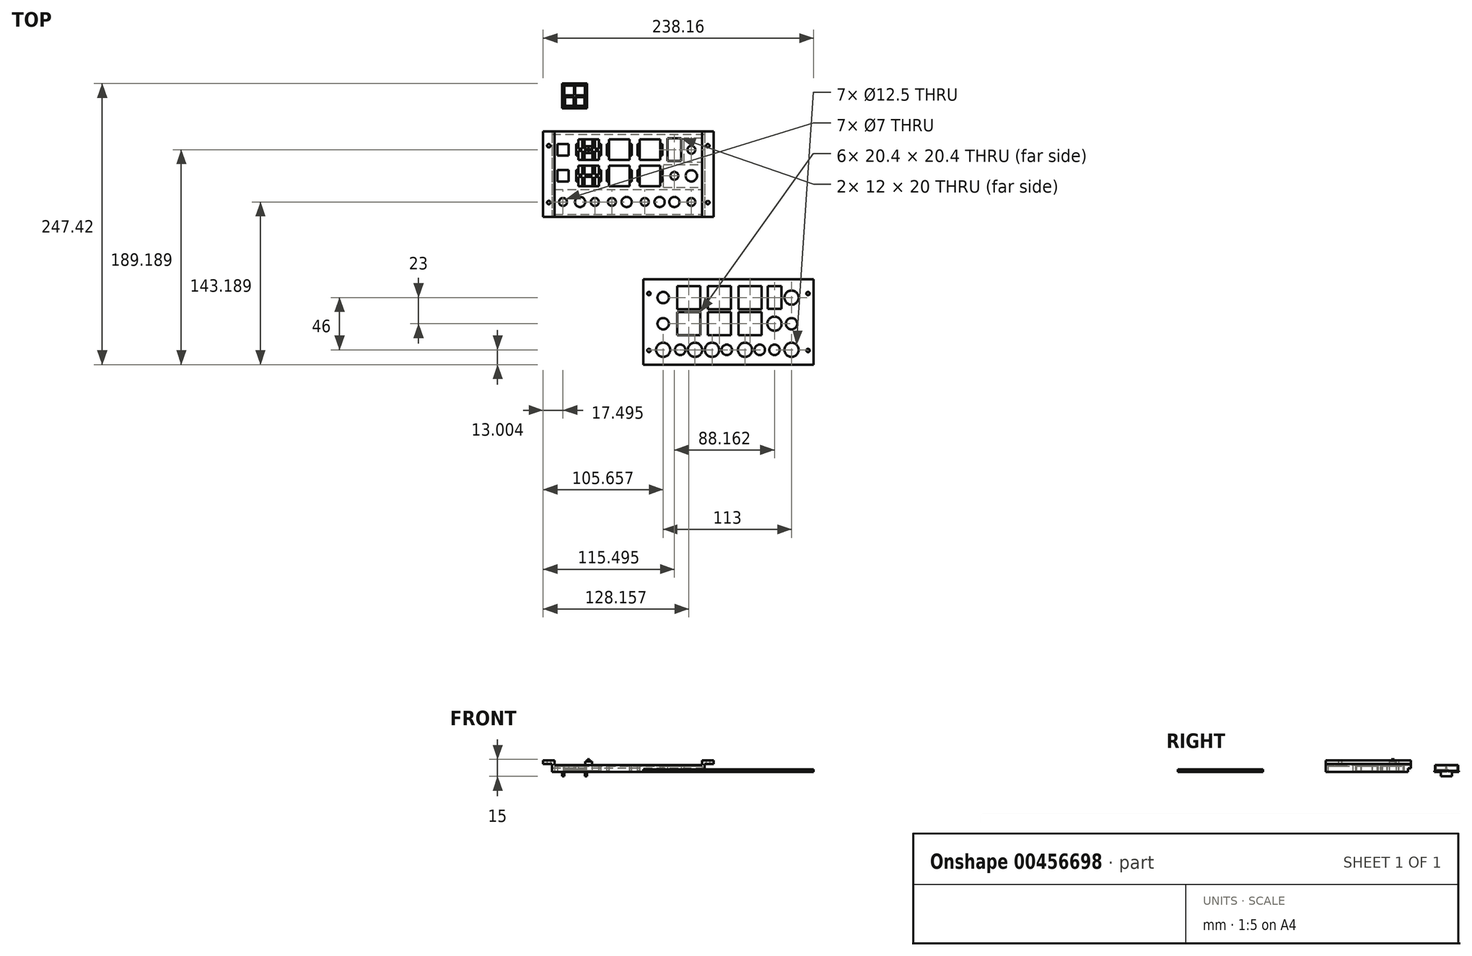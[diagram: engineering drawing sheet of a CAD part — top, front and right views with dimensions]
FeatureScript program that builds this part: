
annotation { "Feature Type Name" : "Feature", "Feature Type Description" : "" }
export const myFeature = defineFeature(function(context is Context, id is Id, definition is map)
    precondition{}
    {
        {
            var Q0;
            Q0=qCreatedBy(makeId("Top.planeOp"),FACE);
            var sketch = newSketch(context, id + "F0", { "sketchPlane" : qUnion([Q0])});
            skLineSegment(sketch, "E0.bottom", {"start": v(0.5, -57.04) * mm, "end": v(-149.5, -57.04) * mm});
            skLineSegment(sketch, "E0.top", {"start": v(0.5, 17.96) * mm, "end": v(-149.5, 17.96) * mm});
            skLineSegment(sketch, "E0.left", {"start": v(0.5, -57.04) * mm, "end": v(0.5, 17.96) * mm});
            skLineSegment(sketch, "E0.right", {"start": v(-149.5, -57.04) * mm, "end": v(-149.5, 17.96) * mm});
            skLineSegment(sketch, "E1.bottom", {"start": v(-99.5, -8.04) * mm, "end": v(-119.5, -8.04) * mm, "construction": true});
            skLineSegment(sketch, "E1.top", {"start": v(-99.5, 11.96) * mm, "end": v(-119.5, 11.96) * mm, "construction": true});
            skLineSegment(sketch, "E1.left", {"start": v(-99.5, -8.04) * mm, "end": v(-99.5, 11.96) * mm, "construction": true});
            skLineSegment(sketch, "E1.right", {"start": v(-119.5, -8.04) * mm, "end": v(-119.5, 11.96) * mm, "construction": true});
            skPoint(sketch, "E1.middle", {"position": v(-109.5, 1.96) * mm});
            skLineSegment(sketch, "E2.bottom", {"start": v(-99.5, -31.04) * mm, "end": v(-119.5, -31.04) * mm, "construction": true});
            skLineSegment(sketch, "E2.top", {"start": v(-99.5, -11.04) * mm, "end": v(-119.5, -11.04) * mm, "construction": true});
            skLineSegment(sketch, "E2.left", {"start": v(-99.5, -31.04) * mm, "end": v(-99.5, -11.04) * mm, "construction": true});
            skLineSegment(sketch, "E2.right", {"start": v(-119.5, -31.04) * mm, "end": v(-119.5, -11.04) * mm, "construction": true});
            skPoint(sketch, "E2.middle", {"position": v(-109.5, -21.04) * mm});
            skCircle(sketch, "E3", {"center": v(-132, -44.04) * mm, "radius": 3.5 * mm});
            skCircle(sketch, "E4", {"center": v(-104, -44.04) * mm, "radius": 3.5 * mm});
            skCircle(sketch, "E5", {"center": v(-89, -44.04) * mm, "radius": 3.5 * mm});
            skLineSegment(sketch, "E6.bottom", {"start": v(-149.5, 17.96) * mm, "end": v(-141.5, 17.96) * mm, "construction": true});
            skLineSegment(sketch, "E6.top", {"start": v(-149.5, -57.04) * mm, "end": v(-141.5, -57.04) * mm, "construction": true});
            skLineSegment(sketch, "E6.left", {"start": v(-149.5, 17.96) * mm, "end": v(-149.5, -57.04) * mm, "construction": true});
            skLineSegment(sketch, "E6.right", {"start": v(-141.5, 17.96) * mm, "end": v(-141.5, -57.04) * mm, "construction": true});
            skLineSegment(sketch, "E7.bottom", {"start": v(0.5, -57.04) * mm, "end": v(-7.5, -57.04) * mm, "construction": true});
            skLineSegment(sketch, "E7.top", {"start": v(0.5, 17.96) * mm, "end": v(-7.5, 17.96) * mm, "construction": true});
            skLineSegment(sketch, "E7.left", {"start": v(0.5, -57.04) * mm, "end": v(0.5, 17.96) * mm, "construction": true});
            skLineSegment(sketch, "E7.right", {"start": v(-7.5, -57.04) * mm, "end": v(-7.5, 17.96) * mm, "construction": true});
            skCircle(sketch, "E8", {"center": v(-117, -44.04) * mm, "radius": 4.5 * mm});
            skCircle(sketch, "E9", {"center": v(-76, -44.04) * mm, "radius": 4.5 * mm});
            skCircle(sketch, "E10", {"center": v(-60, -44.04) * mm, "radius": 3.5 * mm});
            skCircle(sketch, "E11", {"center": v(-47, -44.04) * mm, "radius": 4.5 * mm});
            skCircle(sketch, "E12", {"center": v(-34, -44.04) * mm, "radius": 4.5 * mm});
            skCircle(sketch, "E13", {"center": v(-19, -44.04) * mm, "radius": 3.5 * mm});
            skCircle(sketch, "E14", {"center": v(-34, -21.04) * mm, "radius": 3.5 * mm});
            skLineSegment(sketch, "E15.bottom", {"start": v(-28, -8.04) * mm, "end": v(-40, -8.04) * mm});
            skLineSegment(sketch, "E15.top", {"start": v(-28, 11.96) * mm, "end": v(-40, 11.96) * mm});
            skLineSegment(sketch, "E15.left", {"start": v(-28, -8.04) * mm, "end": v(-28, 11.96) * mm});
            skLineSegment(sketch, "E15.right", {"start": v(-40, -8.04) * mm, "end": v(-40, 11.96) * mm});
            skPoint(sketch, "E15.middle", {"position": v(-34, 1.96) * mm});
            skCircle(sketch, "E16", {"center": v(-19, 1.96) * mm, "radius": 3.5 * mm});
            skCircle(sketch, "E17", {"center": v(-19, -21.04) * mm, "radius": 5 * mm});
            skPoint(sketch, "E18.centerSnap0", {"position": v(-119.5, -21.04) * mm});
            skLineSegment(sketch, "E19.bottom", {"start": v(-100.5, -7.04) * mm, "end": v(-118.5, -7.04) * mm});
            skLineSegment(sketch, "E19.top", {"start": v(-100.5, 10.96) * mm, "end": v(-118.5, 10.96) * mm});
            skLineSegment(sketch, "E19.left", {"start": v(-100.5, -7.04) * mm, "end": v(-100.5, 10.96) * mm});
            skLineSegment(sketch, "E19.right", {"start": v(-118.5, -7.04) * mm, "end": v(-118.5, 10.96) * mm});
            skLineSegment(sketch, "E20.bottom", {"start": v(-100.5, -30.04) * mm, "end": v(-118.5, -30.04) * mm});
            skLineSegment(sketch, "E20.top", {"start": v(-100.5, -12.04) * mm, "end": v(-118.5, -12.04) * mm});
            skLineSegment(sketch, "E20.left", {"start": v(-100.5, -30.04) * mm, "end": v(-100.5, -12.04) * mm});
            skLineSegment(sketch, "E20.right", {"start": v(-118.5, -30.04) * mm, "end": v(-118.5, -12.04) * mm});
            skLineSegment(sketch, "E21.bottom", {"start": v(-100.5, 0.96) * mm, "end": v(-104, 0.96) * mm});
            skLineSegment(sketch, "E21.top", {"start": v(-100.5, 2.96) * mm, "end": v(-104, 2.96) * mm});
            skLineSegment(sketch, "E21.left", {"start": v(-100.5, 0.96) * mm, "end": v(-100.5, 2.96) * mm});
            skLineSegment(sketch, "E21.right", {"start": v(-118.5, 0.96) * mm, "end": v(-118.5, 2.96) * mm});
            skLineSegment(sketch, "E22.bottom", {"start": v(-113, -7.04) * mm, "end": v(-115, -7.04) * mm});
            skLineSegment(sketch, "E22.top", {"start": v(-113, 10.96) * mm, "end": v(-115, 10.96) * mm});
            skLineSegment(sketch, "E22.left", {"start": v(-113, -7.04) * mm, "end": v(-113, 0.96) * mm});
            skLineSegment(sketch, "E22.right", {"start": v(-115, -7.04) * mm, "end": v(-115, 0.96) * mm});
            skPoint(sketch, "E22.middle", {"position": v(-114, 1.96) * mm});
            skLineSegment(sketch, "E23.bottom", {"start": v(-104, -7.04) * mm, "end": v(-106, -7.04) * mm});
            skLineSegment(sketch, "E23.top", {"start": v(-104, 10.96) * mm, "end": v(-106, 10.96) * mm});
            skLineSegment(sketch, "E23.left", {"start": v(-104, -7.04) * mm, "end": v(-104, 0.96) * mm});
            skLineSegment(sketch, "E23.right", {"start": v(-106, -7.04) * mm, "end": v(-106, 0.96) * mm});
            skPoint(sketch, "E23.middle", {"position": v(-105, 1.96) * mm});
            skLineSegment(sketch, "E24.trimOffspring", {"start": v(-115, 2.96) * mm, "end": v(-115, 10.96) * mm});
            skLineSegment(sketch, "E25.trimOffspring", {"start": v(-115, 2.96) * mm, "end": v(-118.5, 2.96) * mm});
            skLineSegment(sketch, "E26.trimOffspring", {"start": v(-113, 2.96) * mm, "end": v(-113, 10.96) * mm});
            skLineSegment(sketch, "E27.trimOffspring", {"start": v(-115, 0.96) * mm, "end": v(-118.5, 0.96) * mm});
            skLineSegment(sketch, "E28.trimOffspring", {"start": v(-106, 2.96) * mm, "end": v(-106, 10.96) * mm});
            skLineSegment(sketch, "E29.trimOffspring", {"start": v(-106, 2.96) * mm, "end": v(-113, 2.96) * mm});
            skLineSegment(sketch, "E30.trimOffspring", {"start": v(-104, 2.96) * mm, "end": v(-104, 10.96) * mm});
            skLineSegment(sketch, "E31.trimOffspring", {"start": v(-106, 0.96) * mm, "end": v(-113, 0.96) * mm});
            skLineSegment(sketch, "E32.bottom", {"start": v(-128.5, -50.54) * mm, "end": v(-135.5, -50.54) * mm, "construction": true});
            skLineSegment(sketch, "E32.top", {"start": v(-128.5, -37.54) * mm, "end": v(-135.5, -37.54) * mm, "construction": true});
            skLineSegment(sketch, "E32.left", {"start": v(-128.5, -50.54) * mm, "end": v(-128.5, -37.54) * mm, "construction": true});
            skLineSegment(sketch, "E32.right", {"start": v(-135.5, -50.54) * mm, "end": v(-135.5, -37.54) * mm, "construction": true});
            skLineSegment(sketch, "E33.bottom", {"start": v(-100.5, -22.04) * mm, "end": v(-104, -22.04) * mm});
            skLineSegment(sketch, "E33.top", {"start": v(-100.5, -20.04) * mm, "end": v(-104, -20.04) * mm});
            skLineSegment(sketch, "E33.left", {"start": v(-100.5, -22.04) * mm, "end": v(-100.5, -20.04) * mm});
            skLineSegment(sketch, "E33.right", {"start": v(-118.5, -22.04) * mm, "end": v(-118.5, -20.04) * mm});
            skLineSegment(sketch, "E34.bottom", {"start": v(-113, -30.04) * mm, "end": v(-115, -30.04) * mm});
            skLineSegment(sketch, "E34.top", {"start": v(-113, -12.04) * mm, "end": v(-115, -12.04) * mm});
            skLineSegment(sketch, "E34.left", {"start": v(-113, -30.04) * mm, "end": v(-113, -22.04) * mm});
            skLineSegment(sketch, "E34.right", {"start": v(-115, -30.04) * mm, "end": v(-115, -22.04) * mm});
            skPoint(sketch, "E34.middle", {"position": v(-114, -21.04) * mm});
            skLineSegment(sketch, "E35.bottom", {"start": v(-104, -30.04) * mm, "end": v(-106, -30.04) * mm});
            skLineSegment(sketch, "E35.top", {"start": v(-104, -12.04) * mm, "end": v(-106, -12.04) * mm});
            skLineSegment(sketch, "E35.left", {"start": v(-104, -30.04) * mm, "end": v(-104, -22.04) * mm});
            skLineSegment(sketch, "E35.right", {"start": v(-106, -30.04) * mm, "end": v(-106, -22.04) * mm});
            skPoint(sketch, "E35.middle", {"position": v(-105, -21.04) * mm});
            skLineSegment(sketch, "E36.trimOffspring", {"start": v(-115, -20.04) * mm, "end": v(-115, -12.04) * mm});
            skLineSegment(sketch, "E37.trimOffspring", {"start": v(-115, -20.04) * mm, "end": v(-118.5, -20.04) * mm});
            skLineSegment(sketch, "E38.trimOffspring", {"start": v(-113, -20.04) * mm, "end": v(-113, -12.04) * mm});
            skLineSegment(sketch, "E39.trimOffspring", {"start": v(-115, -22.04) * mm, "end": v(-118.5, -22.04) * mm});
            skLineSegment(sketch, "E40.trimOffspring", {"start": v(-106, -20.04) * mm, "end": v(-106, -12.04) * mm});
            skLineSegment(sketch, "E41.trimOffspring", {"start": v(-106, -20.04) * mm, "end": v(-113, -20.04) * mm});
            skLineSegment(sketch, "E42.trimOffspring", {"start": v(-104, -20.04) * mm, "end": v(-104, -12.04) * mm});
            skLineSegment(sketch, "E43.trimOffspring", {"start": v(-106, -22.04) * mm, "end": v(-113, -22.04) * mm});
            skLineSegment(sketch, "E44.bottom", {"start": v(-127, -3.04) * mm, "end": v(-137, -3.04) * mm});
            skLineSegment(sketch, "E44.top", {"start": v(-127, 6.96) * mm, "end": v(-137, 6.96) * mm});
            skLineSegment(sketch, "E44.left", {"start": v(-127, -3.04) * mm, "end": v(-127, 6.96) * mm});
            skLineSegment(sketch, "E44.right", {"start": v(-137, -3.04) * mm, "end": v(-137, 6.96) * mm});
            skPoint(sketch, "E44.middle", {"position": v(-132, 1.96) * mm});
            skLineSegment(sketch, "E45.bottom", {"start": v(-127, -26.04) * mm, "end": v(-137, -26.04) * mm});
            skLineSegment(sketch, "E45.top", {"start": v(-127, -16.04) * mm, "end": v(-137, -16.04) * mm});
            skLineSegment(sketch, "E45.left", {"start": v(-127, -26.04) * mm, "end": v(-127, -16.04) * mm});
            skLineSegment(sketch, "E45.right", {"start": v(-137, -26.04) * mm, "end": v(-137, -16.04) * mm});
            skPoint(sketch, "E45.middle", {"position": v(-132, -21.04) * mm});
            skLineSegment(sketch, "E46.bottom", {"start": v(-131, -3.04) * mm, "end": v(-133, -3.04) * mm});
            skLineSegment(sketch, "E46.top", {"start": v(-131, 6.96) * mm, "end": v(-133, 6.96) * mm});
            skLineSegment(sketch, "E46.left", {"start": v(-131, -3.04) * mm, "end": v(-131, 6.96) * mm});
            skLineSegment(sketch, "E46.right", {"start": v(-133, -3.04) * mm, "end": v(-133, 6.96) * mm});
            skLineSegment(sketch, "E47.bottom", {"start": v(-131, -26.04) * mm, "end": v(-133, -26.04) * mm});
            skLineSegment(sketch, "E47.top", {"start": v(-131, -16.04) * mm, "end": v(-133, -16.04) * mm});
            skLineSegment(sketch, "E47.left", {"start": v(-131, -26.04) * mm, "end": v(-131, -16.04) * mm});
            skLineSegment(sketch, "E47.right", {"start": v(-133, -26.04) * mm, "end": v(-133, -16.04) * mm});
            skCircle(sketch, "E48", {"center": v(-144.5, 5.46) * mm, "radius": 1.5 * mm});
            skPoint(sketch, "E48.centerSnap0", {"position": v(-145.5, 17.96) * mm});
            skCircle(sketch, "E49", {"center": v(-144.5, -44.54) * mm, "radius": 1.5 * mm});
            skCircle(sketch, "E50", {"center": v(-4.5, 5.46) * mm, "radius": 1.5 * mm});
            skCircle(sketch, "E51", {"center": v(-4.5, -44.54) * mm, "radius": 1.5 * mm});
            skLineSegment(sketch, "E52.1.0.0", {"start": v(-73.5, 2.96) * mm, "end": v(-77, 2.96) * mm});
            skLineSegment(sketch, "E52.1.0.1", {"start": v(-79, -30.04) * mm, "end": v(-79, -22.04) * mm});
            skLineSegment(sketch, "E52.1.0.2", {"start": v(-79, -22.04) * mm, "end": v(-86, -22.04) * mm});
            skLineSegment(sketch, "E52.1.0.3", {"start": v(-88, -30.04) * mm, "end": v(-88, -22.04) * mm});
            skLineSegment(sketch, "E52.1.0.4", {"start": v(-72.5, -8.04) * mm, "end": v(-72.5, 11.96) * mm, "construction": true});
            skLineSegment(sketch, "E52.1.0.5", {"start": v(-72.5, -8.04) * mm, "end": v(-92.5, -8.04) * mm, "construction": true});
            skLineSegment(sketch, "E52.1.0.6", {"start": v(-72.5, -31.04) * mm, "end": v(-92.5, -31.04) * mm, "construction": true});
            skLineSegment(sketch, "E52.1.0.7", {"start": v(-73.5, -30.04) * mm, "end": v(-73.5, -12.04) * mm});
            skLineSegment(sketch, "E52.1.0.8", {"start": v(-73.5, -7.04) * mm, "end": v(-91.5, -7.04) * mm});
            skLineSegment(sketch, "E52.1.0.9", {"start": v(-79, 2.96) * mm, "end": v(-86, 2.96) * mm});
            skLineSegment(sketch, "E52.1.0.10", {"start": v(-79, -20.04) * mm, "end": v(-86, -20.04) * mm});
            skLineSegment(sketch, "E52.1.0.11", {"start": v(-88, 2.96) * mm, "end": v(-91.5, 2.96) * mm});
            skLineSegment(sketch, "E52.1.0.12", {"start": v(-77, -30.04) * mm, "end": v(-77, -22.04) * mm});
            skLineSegment(sketch, "E52.1.0.13", {"start": v(-86, 2.96) * mm, "end": v(-86, 10.96) * mm});
            skLineSegment(sketch, "E52.1.0.14", {"start": v(-77, -20.04) * mm, "end": v(-77, -12.04) * mm});
            skLineSegment(sketch, "E52.1.0.15", {"start": v(-88, -20.04) * mm, "end": v(-88, -12.04) * mm});
            skLineSegment(sketch, "E52.1.0.16", {"start": v(-79, 2.96) * mm, "end": v(-79, 10.96) * mm});
            skPoint(sketch, "E52.1.0.17", {"position": v(-82.5, -21.04) * mm});
            skLineSegment(sketch, "E52.1.0.18", {"start": v(-73.5, -22.04) * mm, "end": v(-77, -22.04) * mm});
            skLineSegment(sketch, "E52.1.0.19", {"start": v(-88, 0.96) * mm, "end": v(-91.5, 0.96) * mm});
            skLineSegment(sketch, "E52.1.0.20", {"start": v(-72.5, 11.96) * mm, "end": v(-92.5, 11.96) * mm, "construction": true});
            skLineSegment(sketch, "E52.1.0.21", {"start": v(-88, -22.04) * mm, "end": v(-91.5, -22.04) * mm});
            skLineSegment(sketch, "E52.1.0.22", {"start": v(-91.5, -7.04) * mm, "end": v(-91.5, 10.96) * mm});
            skLineSegment(sketch, "E52.1.0.23", {"start": v(-72.5, -11.04) * mm, "end": v(-92.5, -11.04) * mm, "construction": true});
            skLineSegment(sketch, "E52.1.0.24", {"start": v(-92.5, -31.04) * mm, "end": v(-92.5, -11.04) * mm, "construction": true});
            skLineSegment(sketch, "E52.1.0.25", {"start": v(-79, -20.04) * mm, "end": v(-79, -12.04) * mm});
            skLineSegment(sketch, "E52.1.0.26", {"start": v(-92.5, -8.04) * mm, "end": v(-92.5, 11.96) * mm, "construction": true});
            skLineSegment(sketch, "E52.1.0.27", {"start": v(-88, 2.96) * mm, "end": v(-88, 10.96) * mm});
            skLineSegment(sketch, "E52.1.0.28", {"start": v(-72.5, -31.04) * mm, "end": v(-72.5, -11.04) * mm, "construction": true});
            skLineSegment(sketch, "E52.1.0.29", {"start": v(-73.5, -7.04) * mm, "end": v(-73.5, 10.96) * mm});
            skLineSegment(sketch, "E52.1.0.30", {"start": v(-73.5, -30.04) * mm, "end": v(-91.5, -30.04) * mm});
            skLineSegment(sketch, "E52.1.0.31", {"start": v(-77, -7.04) * mm, "end": v(-77, 0.96) * mm});
            skLineSegment(sketch, "E52.1.0.32", {"start": v(-79, -7.04) * mm, "end": v(-79, 0.96) * mm});
            skLineSegment(sketch, "E52.1.0.33", {"start": v(-86, -20.04) * mm, "end": v(-86, -12.04) * mm});
            skLineSegment(sketch, "E52.1.0.34", {"start": v(-73.5, 0.96) * mm, "end": v(-77, 0.96) * mm});
            skLineSegment(sketch, "E52.1.0.35", {"start": v(-73.5, -12.04) * mm, "end": v(-91.5, -12.04) * mm});
            skLineSegment(sketch, "E52.1.0.36", {"start": v(-86, -30.04) * mm, "end": v(-86, -22.04) * mm});
            skLineSegment(sketch, "E52.1.0.37", {"start": v(-77, 2.96) * mm, "end": v(-77, 10.96) * mm});
            skLineSegment(sketch, "E52.1.0.38", {"start": v(-88, -7.04) * mm, "end": v(-88, 0.96) * mm});
            skLineSegment(sketch, "E52.1.0.39", {"start": v(-91.5, -30.04) * mm, "end": v(-91.5, -12.04) * mm});
            skLineSegment(sketch, "E52.1.0.40", {"start": v(-73.5, 10.96) * mm, "end": v(-91.5, 10.96) * mm});
            skLineSegment(sketch, "E52.1.0.41", {"start": v(-73.5, -20.04) * mm, "end": v(-77, -20.04) * mm});
            skPoint(sketch, "E52.1.0.42", {"position": v(-82.5, 1.96) * mm});
            skPoint(sketch, "E52.1.0.43", {"position": v(-92.5, -21.04) * mm});
            skLineSegment(sketch, "E52.1.0.44", {"start": v(-79, 0.96) * mm, "end": v(-86, 0.96) * mm});
            skLineSegment(sketch, "E52.1.0.45", {"start": v(-86, -7.04) * mm, "end": v(-86, 0.96) * mm});
            skLineSegment(sketch, "E52.1.0.46", {"start": v(-73.5, -12.04) * mm, "end": v(-91.5, -12.04) * mm});
            skLineSegment(sketch, "E52.1.0.47", {"start": v(-73.5, -30.04) * mm, "end": v(-73.5, -12.04) * mm});
            skLineSegment(sketch, "E52.1.0.48", {"start": v(-73.5, -30.04) * mm, "end": v(-91.5, -30.04) * mm});
            skPoint(sketch, "E52.1.0.49", {"position": v(-82.5, -21.04) * mm});
            skPoint(sketch, "E52.1.0.50", {"position": v(-82.5, 1.96) * mm});
            skLineSegment(sketch, "E52.1.0.51", {"start": v(-88, -20.04) * mm, "end": v(-91.5, -20.04) * mm});
            skLineSegment(sketch, "E52.1.0.52", {"start": v(-91.5, -30.04) * mm, "end": v(-91.5, -12.04) * mm});
            skPoint(sketch, "E52.1.0.53", {"position": v(-87, 1.96) * mm});
            skLineSegment(sketch, "E52.1.0.54", {"start": v(-91.5, -22.04) * mm, "end": v(-91.5, -20.04) * mm});
            skLineSegment(sketch, "E52.1.0.55", {"start": v(-86, -12.04) * mm, "end": v(-88, -12.04) * mm});
            skLineSegment(sketch, "E52.1.0.56", {"start": v(-91.5, 0.96) * mm, "end": v(-91.5, 2.96) * mm});
            skLineSegment(sketch, "E52.1.0.57", {"start": v(-86, 10.96) * mm, "end": v(-88, 10.96) * mm});
            skLineSegment(sketch, "E52.1.0.58", {"start": v(-86, -30.04) * mm, "end": v(-88, -30.04) * mm});
            skLineSegment(sketch, "E52.1.0.59", {"start": v(-73.5, -22.04) * mm, "end": v(-73.5, -20.04) * mm});
            skPoint(sketch, "E52.1.0.60", {"position": v(-78, -21.04) * mm});
            skLineSegment(sketch, "E52.1.0.61", {"start": v(-77, -7.04) * mm, "end": v(-79, -7.04) * mm});
            skPoint(sketch, "E52.1.0.62", {"position": v(-87, -21.04) * mm});
            skPoint(sketch, "E52.1.0.63", {"position": v(-82.5, -21.04) * mm});
            skLineSegment(sketch, "E52.1.0.64", {"start": v(-77, -30.04) * mm, "end": v(-79, -30.04) * mm});
            skLineSegment(sketch, "E52.1.0.65", {"start": v(-73.5, 0.96) * mm, "end": v(-73.5, 2.96) * mm});
            skPoint(sketch, "E52.1.0.66", {"position": v(-82.5, 1.96) * mm});
            skLineSegment(sketch, "E52.1.0.67", {"start": v(-86, -7.04) * mm, "end": v(-88, -7.04) * mm});
            skLineSegment(sketch, "E52.1.0.68", {"start": v(-77, 10.96) * mm, "end": v(-79, 10.96) * mm});
            skPoint(sketch, "E52.1.0.69", {"position": v(-78, 1.96) * mm});
            skLineSegment(sketch, "E52.1.0.70", {"start": v(-77, -12.04) * mm, "end": v(-79, -12.04) * mm});
            skPoint(sketch, "E52.1.0.71", {"position": v(-82.5, -21.04) * mm});
            skPoint(sketch, "E52.1.0.72", {"position": v(-82.5, -21.04) * mm});
            skLineSegment(sketch, "E52.2.0.0", {"start": v(-46.5, 2.96) * mm, "end": v(-50, 2.96) * mm});
            skLineSegment(sketch, "E52.2.0.1", {"start": v(-52, -30.04) * mm, "end": v(-52, -22.04) * mm});
            skLineSegment(sketch, "E52.2.0.2", {"start": v(-52, -22.04) * mm, "end": v(-59, -22.04) * mm});
            skLineSegment(sketch, "E52.2.0.3", {"start": v(-61, -30.04) * mm, "end": v(-61, -22.04) * mm});
            skLineSegment(sketch, "E52.2.0.4", {"start": v(-45.5, -8.04) * mm, "end": v(-45.5, 11.96) * mm, "construction": true});
            skLineSegment(sketch, "E52.2.0.5", {"start": v(-45.5, -8.04) * mm, "end": v(-65.5, -8.04) * mm, "construction": true});
            skLineSegment(sketch, "E52.2.0.6", {"start": v(-45.5, -31.04) * mm, "end": v(-65.5, -31.04) * mm, "construction": true});
            skLineSegment(sketch, "E52.2.0.7", {"start": v(-46.5, -30.04) * mm, "end": v(-46.5, -12.04) * mm});
            skLineSegment(sketch, "E52.2.0.8", {"start": v(-46.5, -7.04) * mm, "end": v(-64.5, -7.04) * mm});
            skLineSegment(sketch, "E52.2.0.9", {"start": v(-52, 2.96) * mm, "end": v(-59, 2.96) * mm});
            skLineSegment(sketch, "E52.2.0.10", {"start": v(-52, -20.04) * mm, "end": v(-59, -20.04) * mm});
            skLineSegment(sketch, "E52.2.0.11", {"start": v(-61, 2.96) * mm, "end": v(-64.5, 2.96) * mm});
            skLineSegment(sketch, "E52.2.0.12", {"start": v(-50, -30.04) * mm, "end": v(-50, -22.04) * mm});
            skLineSegment(sketch, "E52.2.0.13", {"start": v(-59, 2.96) * mm, "end": v(-59, 10.96) * mm});
            skLineSegment(sketch, "E52.2.0.14", {"start": v(-50, -20.04) * mm, "end": v(-50, -12.04) * mm});
            skLineSegment(sketch, "E52.2.0.15", {"start": v(-61, -20.04) * mm, "end": v(-61, -12.04) * mm});
            skLineSegment(sketch, "E52.2.0.16", {"start": v(-52, 2.96) * mm, "end": v(-52, 10.96) * mm});
            skPoint(sketch, "E52.2.0.17", {"position": v(-55.5, -21.04) * mm});
            skLineSegment(sketch, "E52.2.0.18", {"start": v(-46.5, -22.04) * mm, "end": v(-50, -22.04) * mm});
            skLineSegment(sketch, "E52.2.0.19", {"start": v(-61, 0.96) * mm, "end": v(-64.5, 0.96) * mm});
            skLineSegment(sketch, "E52.2.0.20", {"start": v(-45.5, 11.96) * mm, "end": v(-65.5, 11.96) * mm, "construction": true});
            skLineSegment(sketch, "E52.2.0.21", {"start": v(-61, -22.04) * mm, "end": v(-64.5, -22.04) * mm});
            skLineSegment(sketch, "E52.2.0.22", {"start": v(-64.5, -7.04) * mm, "end": v(-64.5, 10.96) * mm});
            skLineSegment(sketch, "E52.2.0.23", {"start": v(-45.5, -11.04) * mm, "end": v(-65.5, -11.04) * mm, "construction": true});
            skLineSegment(sketch, "E52.2.0.24", {"start": v(-65.5, -31.04) * mm, "end": v(-65.5, -11.04) * mm, "construction": true});
            skLineSegment(sketch, "E52.2.0.25", {"start": v(-52, -20.04) * mm, "end": v(-52, -12.04) * mm});
            skLineSegment(sketch, "E52.2.0.26", {"start": v(-65.5, -8.04) * mm, "end": v(-65.5, 11.96) * mm, "construction": true});
            skLineSegment(sketch, "E52.2.0.27", {"start": v(-61, 2.96) * mm, "end": v(-61, 10.96) * mm});
            skLineSegment(sketch, "E52.2.0.28", {"start": v(-45.5, -31.04) * mm, "end": v(-45.5, -11.04) * mm, "construction": true});
            skLineSegment(sketch, "E52.2.0.29", {"start": v(-46.5, -7.04) * mm, "end": v(-46.5, 10.96) * mm});
            skLineSegment(sketch, "E52.2.0.30", {"start": v(-46.5, -30.04) * mm, "end": v(-64.5, -30.04) * mm});
            skLineSegment(sketch, "E52.2.0.31", {"start": v(-50, -7.04) * mm, "end": v(-50, 0.96) * mm});
            skLineSegment(sketch, "E52.2.0.32", {"start": v(-52, -7.04) * mm, "end": v(-52, 0.96) * mm});
            skLineSegment(sketch, "E52.2.0.33", {"start": v(-59, -20.04) * mm, "end": v(-59, -12.04) * mm});
            skLineSegment(sketch, "E52.2.0.34", {"start": v(-46.5, 0.96) * mm, "end": v(-50, 0.96) * mm});
            skLineSegment(sketch, "E52.2.0.35", {"start": v(-46.5, -12.04) * mm, "end": v(-64.5, -12.04) * mm});
            skLineSegment(sketch, "E52.2.0.36", {"start": v(-59, -30.04) * mm, "end": v(-59, -22.04) * mm});
            skLineSegment(sketch, "E52.2.0.37", {"start": v(-50, 2.96) * mm, "end": v(-50, 10.96) * mm});
            skLineSegment(sketch, "E52.2.0.38", {"start": v(-61, -7.04) * mm, "end": v(-61, 0.96) * mm});
            skLineSegment(sketch, "E52.2.0.39", {"start": v(-64.5, -30.04) * mm, "end": v(-64.5, -12.04) * mm});
            skLineSegment(sketch, "E52.2.0.40", {"start": v(-46.5, 10.96) * mm, "end": v(-64.5, 10.96) * mm});
            skLineSegment(sketch, "E52.2.0.41", {"start": v(-46.5, -20.04) * mm, "end": v(-50, -20.04) * mm});
            skPoint(sketch, "E52.2.0.42", {"position": v(-55.5, 1.96) * mm});
            skPoint(sketch, "E52.2.0.43", {"position": v(-65.5, -21.04) * mm});
            skLineSegment(sketch, "E52.2.0.44", {"start": v(-52, 0.96) * mm, "end": v(-59, 0.96) * mm});
            skLineSegment(sketch, "E52.2.0.45", {"start": v(-59, -7.04) * mm, "end": v(-59, 0.96) * mm});
            skLineSegment(sketch, "E52.2.0.46", {"start": v(-46.5, -12.04) * mm, "end": v(-64.5, -12.04) * mm});
            skLineSegment(sketch, "E52.2.0.47", {"start": v(-46.5, -30.04) * mm, "end": v(-46.5, -12.04) * mm});
            skLineSegment(sketch, "E52.2.0.48", {"start": v(-46.5, -30.04) * mm, "end": v(-64.5, -30.04) * mm});
            skPoint(sketch, "E52.2.0.49", {"position": v(-55.5, -21.04) * mm});
            skPoint(sketch, "E52.2.0.50", {"position": v(-55.5, 1.96) * mm});
            skLineSegment(sketch, "E52.2.0.51", {"start": v(-61, -20.04) * mm, "end": v(-64.5, -20.04) * mm});
            skLineSegment(sketch, "E52.2.0.52", {"start": v(-64.5, -30.04) * mm, "end": v(-64.5, -12.04) * mm});
            skPoint(sketch, "E52.2.0.53", {"position": v(-60, 1.96) * mm});
            skLineSegment(sketch, "E52.2.0.54", {"start": v(-64.5, -22.04) * mm, "end": v(-64.5, -20.04) * mm});
            skLineSegment(sketch, "E52.2.0.55", {"start": v(-59, -12.04) * mm, "end": v(-61, -12.04) * mm});
            skLineSegment(sketch, "E52.2.0.56", {"start": v(-64.5, 0.96) * mm, "end": v(-64.5, 2.96) * mm});
            skLineSegment(sketch, "E52.2.0.57", {"start": v(-59, 10.96) * mm, "end": v(-61, 10.96) * mm});
            skLineSegment(sketch, "E52.2.0.58", {"start": v(-59, -30.04) * mm, "end": v(-61, -30.04) * mm});
            skLineSegment(sketch, "E52.2.0.59", {"start": v(-46.5, -22.04) * mm, "end": v(-46.5, -20.04) * mm});
            skPoint(sketch, "E52.2.0.60", {"position": v(-51, -21.04) * mm});
            skLineSegment(sketch, "E52.2.0.61", {"start": v(-50, -7.04) * mm, "end": v(-52, -7.04) * mm});
            skPoint(sketch, "E52.2.0.62", {"position": v(-60, -21.04) * mm});
            skPoint(sketch, "E52.2.0.63", {"position": v(-55.5, -21.04) * mm});
            skLineSegment(sketch, "E52.2.0.64", {"start": v(-50, -30.04) * mm, "end": v(-52, -30.04) * mm});
            skLineSegment(sketch, "E52.2.0.65", {"start": v(-46.5, 0.96) * mm, "end": v(-46.5, 2.96) * mm});
            skPoint(sketch, "E52.2.0.66", {"position": v(-55.5, 1.96) * mm});
            skLineSegment(sketch, "E52.2.0.67", {"start": v(-59, -7.04) * mm, "end": v(-61, -7.04) * mm});
            skLineSegment(sketch, "E52.2.0.68", {"start": v(-50, 10.96) * mm, "end": v(-52, 10.96) * mm});
            skPoint(sketch, "E52.2.0.69", {"position": v(-51, 1.96) * mm});
            skLineSegment(sketch, "E52.2.0.70", {"start": v(-50, -12.04) * mm, "end": v(-52, -12.04) * mm});
            skPoint(sketch, "E52.2.0.71", {"position": v(-55.5, -21.04) * mm});
            skPoint(sketch, "E52.2.0.72", {"position": v(-55.5, -21.04) * mm});
            skLineSegment(sketch, "E52.direction1", {"start": v(-119.5, -31.04) * mm, "end": v(-92.5, -31.04) * mm, "construction": true});
            skSolve(sketch);
        }
        {
            var Q0;
            Q0=qCreatedBy(makeId("Top.planeOp"),FACE);
            var sketch = newSketch(context, id + "F1", { "sketchPlane" : qUnion([Q0])});
            skLineSegment(sketch, "E53.bottom", {"start": v(88.66, -187.23) * mm, "end": v(-61.34, -187.23) * mm});
            skLineSegment(sketch, "E53.top", {"start": v(88.66, -112.23) * mm, "end": v(-61.34, -112.23) * mm});
            skLineSegment(sketch, "E53.left", {"start": v(88.66, -187.23) * mm, "end": v(88.66, -112.23) * mm});
            skLineSegment(sketch, "E53.right", {"start": v(-61.34, -187.23) * mm, "end": v(-61.34, -112.23) * mm});
            skLineSegment(sketch, "E54.bottom", {"start": v(-11.14, -138.43) * mm, "end": v(-31.54, -138.43) * mm});
            skLineSegment(sketch, "E54.top", {"start": v(-11.14, -118.03) * mm, "end": v(-31.54, -118.03) * mm});
            skLineSegment(sketch, "E54.left", {"start": v(-11.14, -138.43) * mm, "end": v(-11.14, -118.03) * mm});
            skLineSegment(sketch, "E54.right", {"start": v(-31.54, -138.43) * mm, "end": v(-31.54, -118.03) * mm});
            skLineSegment(sketch, "E55.bottom", {"start": v(-11.14, -161.43) * mm, "end": v(-31.54, -161.43) * mm});
            skLineSegment(sketch, "E55.top", {"start": v(-11.14, -141.03) * mm, "end": v(-31.54, -141.03) * mm});
            skLineSegment(sketch, "E55.left", {"start": v(-11.14, -161.43) * mm, "end": v(-11.14, -141.03) * mm});
            skLineSegment(sketch, "E55.right", {"start": v(-31.54, -161.43) * mm, "end": v(-31.54, -141.03) * mm});
            skCircle(sketch, "E56", {"center": v(-43.84, -174.23) * mm, "radius": 3.5 * mm, "construction": true});
            skCircle(sketch, "E57", {"center": v(-15.84, -174.23) * mm, "radius": 3.5 * mm, "construction": true});
            skCircle(sketch, "E58", {"center": v(-0.84, -174.23) * mm, "radius": 3.5 * mm, "construction": true});
            skLineSegment(sketch, "E59.bottom", {"start": v(-61.34, -112.23) * mm, "end": v(-53.34, -112.23) * mm, "construction": true});
            skLineSegment(sketch, "E59.top", {"start": v(-61.34, -187.23) * mm, "end": v(-53.34, -187.23) * mm, "construction": true});
            skLineSegment(sketch, "E59.left", {"start": v(-61.34, -112.23) * mm, "end": v(-61.34, -187.23) * mm, "construction": true});
            skLineSegment(sketch, "E59.right", {"start": v(-53.34, -112.23) * mm, "end": v(-53.34, -187.23) * mm, "construction": true});
            skLineSegment(sketch, "E60.bottom", {"start": v(88.66, -187.23) * mm, "end": v(80.66, -187.23) * mm, "construction": true});
            skLineSegment(sketch, "E60.top", {"start": v(88.66, -112.23) * mm, "end": v(80.66, -112.23) * mm, "construction": true});
            skLineSegment(sketch, "E60.left", {"start": v(88.66, -187.23) * mm, "end": v(88.66, -112.23) * mm, "construction": true});
            skLineSegment(sketch, "E60.right", {"start": v(80.66, -187.23) * mm, "end": v(80.66, -112.23) * mm, "construction": true});
            skCircle(sketch, "E61", {"center": v(-28.84, -174.23) * mm, "radius": 4.6 * mm});
            skCircle(sketch, "E62", {"center": v(12.16, -174.23) * mm, "radius": 4.6 * mm});
            skCircle(sketch, "E63", {"center": v(28.16, -174.23) * mm, "radius": 3.5 * mm, "construction": true});
            skCircle(sketch, "E64", {"center": v(41.16, -174.23) * mm, "radius": 4.6 * mm});
            skCircle(sketch, "E65", {"center": v(54.16, -174.23) * mm, "radius": 4.6 * mm});
            skCircle(sketch, "E66", {"center": v(69.16, -174.23) * mm, "radius": 3.5 * mm, "construction": true});
            skCircle(sketch, "E67", {"center": v(54.16, -151.23) * mm, "radius": 3.5 * mm, "construction": true});
            skLineSegment(sketch, "E68.bottom", {"start": v(60.16, -138.23) * mm, "end": v(48.16, -138.23) * mm});
            skLineSegment(sketch, "E68.top", {"start": v(60.16, -118.23) * mm, "end": v(48.16, -118.23) * mm});
            skLineSegment(sketch, "E68.left", {"start": v(60.16, -138.23) * mm, "end": v(60.16, -118.23) * mm});
            skLineSegment(sketch, "E68.right", {"start": v(48.16, -138.23) * mm, "end": v(48.16, -118.23) * mm});
            skPoint(sketch, "E68.middle", {"position": v(54.16, -128.23) * mm});
            skCircle(sketch, "E69", {"center": v(69.16, -128.23) * mm, "radius": 3.5 * mm, "construction": true});
            skCircle(sketch, "E70", {"center": v(69.16, -151.23) * mm, "radius": 5 * mm});
            skLineSegment(sketch, "E71.bottom", {"start": v(-40.34, -180.73) * mm, "end": v(-47.34, -180.73) * mm, "construction": true});
            skLineSegment(sketch, "E71.top", {"start": v(-40.34, -167.73) * mm, "end": v(-47.34, -167.73) * mm, "construction": true});
            skLineSegment(sketch, "E71.left", {"start": v(-40.34, -180.73) * mm, "end": v(-40.34, -167.73) * mm, "construction": true});
            skLineSegment(sketch, "E71.right", {"start": v(-47.34, -180.73) * mm, "end": v(-47.34, -167.73) * mm, "construction": true});
            skLineSegment(sketch, "E72.bottom", {"start": v(-38.84, -133.23) * mm, "end": v(-48.84, -133.23) * mm, "construction": true});
            skLineSegment(sketch, "E72.top", {"start": v(-38.84, -123.23) * mm, "end": v(-48.84, -123.23) * mm, "construction": true});
            skLineSegment(sketch, "E72.left", {"start": v(-38.84, -133.23) * mm, "end": v(-38.84, -123.23) * mm, "construction": true});
            skLineSegment(sketch, "E72.right", {"start": v(-48.84, -133.23) * mm, "end": v(-48.84, -123.23) * mm, "construction": true});
            skPoint(sketch, "E72.middle", {"position": v(-43.84, -128.23) * mm});
            skLineSegment(sketch, "E73.bottom", {"start": v(-38.84, -156.23) * mm, "end": v(-48.84, -156.23) * mm, "construction": true});
            skLineSegment(sketch, "E73.top", {"start": v(-38.84, -146.23) * mm, "end": v(-48.84, -146.23) * mm, "construction": true});
            skLineSegment(sketch, "E73.left", {"start": v(-38.84, -156.23) * mm, "end": v(-38.84, -146.23) * mm, "construction": true});
            skLineSegment(sketch, "E73.right", {"start": v(-48.84, -156.23) * mm, "end": v(-48.84, -146.23) * mm, "construction": true});
            skPoint(sketch, "E73.middle", {"position": v(-43.84, -151.23) * mm});
            skLineSegment(sketch, "E74.bottom", {"start": v(-42.84, -133.23) * mm, "end": v(-44.84, -133.23) * mm});
            skLineSegment(sketch, "E74.top", {"start": v(-42.84, -123.23) * mm, "end": v(-44.84, -123.23) * mm});
            skLineSegment(sketch, "E74.left", {"start": v(-42.84, -133.23) * mm, "end": v(-42.84, -123.23) * mm});
            skLineSegment(sketch, "E74.right", {"start": v(-44.84, -133.23) * mm, "end": v(-44.84, -123.23) * mm});
            skLineSegment(sketch, "E75.bottom", {"start": v(-42.84, -156.23) * mm, "end": v(-44.84, -156.23) * mm});
            skLineSegment(sketch, "E75.top", {"start": v(-42.84, -146.23) * mm, "end": v(-44.84, -146.23) * mm});
            skLineSegment(sketch, "E75.left", {"start": v(-42.84, -156.23) * mm, "end": v(-42.84, -146.23) * mm});
            skLineSegment(sketch, "E75.right", {"start": v(-44.84, -156.23) * mm, "end": v(-44.84, -146.23) * mm});
            skCircle(sketch, "E76", {"center": v(-56.34, -124.73) * mm, "radius": 1.5 * mm});
            skPoint(sketch, "E76.centerSnap0", {"position": v(-57.34, -112.23) * mm});
            skCircle(sketch, "E77", {"center": v(-43.84, -128.23) * mm, "radius": 5 * mm});
            skCircle(sketch, "E78", {"center": v(-43.84, -151.23) * mm, "radius": 5 * mm});
            skCircle(sketch, "E79", {"center": v(-43.84, -174.23) * mm, "radius": 6.25 * mm});
            skCircle(sketch, "E80", {"center": v(-15.84, -174.23) * mm, "radius": 6.25 * mm});
            skCircle(sketch, "E81", {"center": v(-0.84, -174.23) * mm, "radius": 6.25 * mm});
            skCircle(sketch, "E82", {"center": v(28.16, -174.23) * mm, "radius": 6.25 * mm});
            skCircle(sketch, "E83", {"center": v(69.16, -174.23) * mm, "radius": 6.25 * mm});
            skCircle(sketch, "E84", {"center": v(54.16, -151.23) * mm, "radius": 6.25 * mm});
            skCircle(sketch, "E85", {"center": v(69.16, -128.23) * mm, "radius": 6.25 * mm});
            skCircle(sketch, "E86", {"center": v(-56.34, -174.73) * mm, "radius": 1.5 * mm});
            skCircle(sketch, "E87", {"center": v(83.66, -124.73) * mm, "radius": 1.5 * mm});
            skCircle(sketch, "E88", {"center": v(83.66, -174.73) * mm, "radius": 1.5 * mm});
            skLineSegment(sketch, "E89.bottom", {"start": v(-53.34, -112.23) * mm, "end": v(-51.34, -112.23) * mm, "construction": true});
            skLineSegment(sketch, "E89.top", {"start": v(-53.34, -187.23) * mm, "end": v(-51.34, -187.23) * mm, "construction": true});
            skLineSegment(sketch, "E89.right", {"start": v(-51.34, -112.23) * mm, "end": v(-51.34, -187.23) * mm, "construction": true});
            skLineSegment(sketch, "E90.bottom", {"start": v(80.66, -112.23) * mm, "end": v(78.66, -112.23) * mm, "construction": true});
            skLineSegment(sketch, "E90.top", {"start": v(80.66, -187.23) * mm, "end": v(78.66, -187.23) * mm, "construction": true});
            skLineSegment(sketch, "E90.left", {"start": v(80.66, -112.23) * mm, "end": v(80.66, -187.23) * mm, "construction": true});
            skLineSegment(sketch, "E90.right", {"start": v(78.66, -112.23) * mm, "end": v(78.66, -187.23) * mm, "construction": true});
            skLineSegment(sketch, "E91.1.0.0", {"start": v(15.86, -138.43) * mm, "end": v(-4.54, -138.43) * mm});
            skLineSegment(sketch, "E91.1.0.1", {"start": v(15.86, -118.03) * mm, "end": v(-4.54, -118.03) * mm});
            skLineSegment(sketch, "E91.1.0.2", {"start": v(15.86, -138.43) * mm, "end": v(15.86, -118.03) * mm});
            skLineSegment(sketch, "E91.1.0.3", {"start": v(-4.54, -138.43) * mm, "end": v(-4.54, -118.03) * mm});
            skLineSegment(sketch, "E91.2.0.0", {"start": v(42.86, -138.43) * mm, "end": v(22.46, -138.43) * mm});
            skLineSegment(sketch, "E91.2.0.1", {"start": v(42.86, -118.03) * mm, "end": v(22.46, -118.03) * mm});
            skLineSegment(sketch, "E91.2.0.2", {"start": v(42.86, -138.43) * mm, "end": v(42.86, -118.03) * mm});
            skLineSegment(sketch, "E91.2.0.3", {"start": v(22.46, -138.43) * mm, "end": v(22.46, -118.03) * mm});
            skLineSegment(sketch, "E91.direction1", {"start": v(-31.54, -138.43) * mm, "end": v(-4.54, -138.43) * mm, "construction": true});
            skLineSegment(sketch, "E92.1.0.0", {"start": v(-4.54, -161.43) * mm, "end": v(-4.54, -141.03) * mm});
            skLineSegment(sketch, "E92.1.0.1", {"start": v(15.86, -161.43) * mm, "end": v(15.86, -141.03) * mm});
            skLineSegment(sketch, "E92.1.0.2", {"start": v(15.86, -141.03) * mm, "end": v(-4.54, -141.03) * mm});
            skLineSegment(sketch, "E92.1.0.3", {"start": v(15.86, -161.43) * mm, "end": v(-4.54, -161.43) * mm});
            skLineSegment(sketch, "E92.2.0.0", {"start": v(22.46, -161.43) * mm, "end": v(22.46, -141.03) * mm});
            skLineSegment(sketch, "E92.2.0.1", {"start": v(42.86, -161.43) * mm, "end": v(42.86, -141.03) * mm});
            skLineSegment(sketch, "E92.2.0.2", {"start": v(42.86, -141.03) * mm, "end": v(22.46, -141.03) * mm});
            skLineSegment(sketch, "E92.2.0.3", {"start": v(42.86, -161.43) * mm, "end": v(22.46, -161.43) * mm});
            skLineSegment(sketch, "E92.direction1", {"start": v(-31.54, -161.43) * mm, "end": v(-4.54, -161.43) * mm, "construction": true});
            skSolve(sketch);
        }
        {
            var Q0;
            Q0=makeQuery(id+"F0.imprint","IMPRINT",FACE,{"disambiguationData":[TD([[makeQuery(id+"F0.imprint","IMPRINT",EDGE,{"derivedFrom":sQuery(id+"F0.wireOp",EDGE,"E0.bottom")}),-1.0]])]});
            var Q1;
            Q1=makeQuery(id+"F0.imprint","IMPRINT",FACE,{"disambiguationData":[TD([[makeQuery(id+"F0.imprint","IMPRINT",EDGE,{"derivedFrom":sQuery(id+"F0.wireOp",EDGE,"E21.bottom")}),-1.0]])]});
            var Q2;
            Q2=makeQuery(id+"F0.imprint","IMPRINT",FACE,{"disambiguationData":[TD([[makeQuery(id+"F0.imprint","IMPRINT",EDGE,{"derivedFrom":sQuery(id+"F0.wireOp",EDGE,"E33.bottom")}),-1.0]])]});
            var Q3;
            Q3=makeQuery(id+"F0.imprint","IMPRINT",FACE,{"disambiguationData":[TD([[makeQuery(id+"F0.imprint","IMPRINT",EDGE,{"derivedFrom":sQuery(id+"F0.wireOp",EDGE,"7093700b-8509-4908-bad7-ce82e1b1d340.1.0.0")}),-1.0]])]});
            var Q4;
            Q4=makeQuery(id+"F0.imprint","IMPRINT",FACE,{"disambiguationData":[TD([[makeQuery(id+"F0.imprint","IMPRINT",EDGE,{"derivedFrom":sQuery(id+"F0.wireOp",EDGE,"7093700b-8509-4908-bad7-ce82e1b1d340.2.0.0")}),-1.0]])]});
            var Q5;
            {var subQ3=sQuery(id+"F0.wireOp",EDGE,"c973f7c2-3bf7-4545-afce-7af64f458de9.2.0.0");Q5=makeQuery(id+"F0.imprint","IMPRINT",FACE,{"disambiguationData":[TD([[makeQuery(id+"F0.imprint","IMPRINT",EDGE,{"derivedFrom":subQ3}),1.0]])]});}
            var Q6;
            {var subQ3=sQuery(id+"F0.wireOp",EDGE,"c973f7c2-3bf7-4545-afce-7af64f458de9.1.0.0");Q6=makeQuery(id+"F0.imprint","IMPRINT",FACE,{"disambiguationData":[TD([[makeQuery(id+"F0.imprint","IMPRINT",EDGE,{"derivedFrom":subQ3}),1.0]])]});}
            var Q7;
            Q7=makeQuery(id+"F0.imprint","IMPRINT",FACE,{"disambiguationData":[TD([[makeQuery(id+"F0.imprint","IMPRINT",EDGE,{"derivedFrom":sQuery(id+"F0.wireOp",EDGE,"E46.bottom")}),-1.0]])]});
            var Q8;
            Q8=makeQuery(id+"F0.imprint","IMPRINT",FACE,{"disambiguationData":[TD([[makeQuery(id+"F0.imprint","IMPRINT",EDGE,{"derivedFrom":sQuery(id+"F0.wireOp",EDGE,"E47.bottom")}),-1.0]])]});
            extrude(context, id + "F2", {"entities" : qUnion([Q0, Q1, Q2, Q3, Q4, Q5, Q6, Q7, Q8]), "depth" : 1 * mm});
        }
        {
            var Q0;
            Q0=makeQuery(id+"F2.opExtrude","CAP_FACE",FACE,{"disambiguationData":[OSD([sQuery(id+"F0.wireOp",EDGE,"E0.bottom"),sQuery(id+"F0.wireOp",EDGE,"E0.top"),sQuery(id+"F0.wireOp",EDGE,"E0.left"),sQuery(id+"F0.wireOp",EDGE,"E0.right"),sQuery(id+"F0.wireOp",EDGE,"E3"),sQuery(id+"F0.wireOp",EDGE,"E4"),sQuery(id+"F0.wireOp",EDGE,"E5"),sQuery(id+"F0.wireOp",EDGE,"E8"),sQuery(id+"F0.wireOp",EDGE,"E9"),sQuery(id+"F0.wireOp",EDGE,"E10"),sQuery(id+"F0.wireOp",EDGE,"E11"),sQuery(id+"F0.wireOp",EDGE,"E12"),sQuery(id+"F0.wireOp",EDGE,"E13"),sQuery(id+"F0.wireOp",EDGE,"E14"),sQuery(id+"F0.wireOp",EDGE,"E15.bottom"),sQuery(id+"F0.wireOp",EDGE,"E15.top"),sQuery(id+"F0.wireOp",EDGE,"E15.left"),sQuery(id+"F0.wireOp",EDGE,"E15.right"),sQuery(id+"F0.wireOp",EDGE,"E16"),sQuery(id+"F0.wireOp",EDGE,"E17"),sQuery(id+"F0.wireOp",EDGE,"E19.bottom"),sQuery(id+"F0.wireOp",EDGE,"E19.top"),sQuery(id+"F0.wireOp",EDGE,"E19.left"),sQuery(id+"F0.wireOp",EDGE,"E19.right"),sQuery(id+"F0.wireOp",EDGE,"E21.bottom"),sQuery(id+"F0.wireOp",EDGE,"E21.top"),sQuery(id+"F0.wireOp",EDGE,"E22.left"),sQuery(id+"F0.wireOp",EDGE,"E22.right"),sQuery(id+"F0.wireOp",EDGE,"E23.left"),sQuery(id+"F0.wireOp",EDGE,"E23.right"),sQuery(id+"F0.wireOp",EDGE,"E24.trimOffspring"),sQuery(id+"F0.wireOp",EDGE,"E25.trimOffspring"),sQuery(id+"F0.wireOp",EDGE,"E26.trimOffspring"),sQuery(id+"F0.wireOp",EDGE,"E27.trimOffspring"),sQuery(id+"F0.wireOp",EDGE,"E28.trimOffspring"),sQuery(id+"F0.wireOp",EDGE,"E29.trimOffspring"),sQuery(id+"F0.wireOp",EDGE,"E30.trimOffspring"),sQuery(id+"F0.wireOp",EDGE,"E31.trimOffspring"),sQuery(id+"F0.wireOp",EDGE,"E20.bottom"),sQuery(id+"F0.wireOp",EDGE,"E20.top"),sQuery(id+"F0.wireOp",EDGE,"E20.left"),sQuery(id+"F0.wireOp",EDGE,"E20.right"),sQuery(id+"F0.wireOp",EDGE,"E33.bottom"),sQuery(id+"F0.wireOp",EDGE,"E33.top"),sQuery(id+"F0.wireOp",EDGE,"E34.left"),sQuery(id+"F0.wireOp",EDGE,"E34.right"),sQuery(id+"F0.wireOp",EDGE,"E35.left"),sQuery(id+"F0.wireOp",EDGE,"E35.right"),sQuery(id+"F0.wireOp",EDGE,"E36.trimOffspring"),sQuery(id+"F0.wireOp",EDGE,"E37.trimOffspring"),sQuery(id+"F0.wireOp",EDGE,"E38.trimOffspring"),sQuery(id+"F0.wireOp",EDGE,"E39.trimOffspring"),sQuery(id+"F0.wireOp",EDGE,"E40.trimOffspring"),sQuery(id+"F0.wireOp",EDGE,"E41.trimOffspring"),sQuery(id+"F0.wireOp",EDGE,"E42.trimOffspring"),sQuery(id+"F0.wireOp",EDGE,"E43.trimOffspring"),sQuery(id+"F0.wireOp",EDGE,"E44.bottom"),sQuery(id+"F0.wireOp",EDGE,"E44.top"),sQuery(id+"F0.wireOp",EDGE,"E44.left"),sQuery(id+"F0.wireOp",EDGE,"E44.right"),sQuery(id+"F0.wireOp",EDGE,"E45.bottom"),sQuery(id+"F0.wireOp",EDGE,"E45.top"),sQuery(id+"F0.wireOp",EDGE,"E45.left"),sQuery(id+"F0.wireOp",EDGE,"E45.right"),sQuery(id+"F0.wireOp",EDGE,"7093700b-8509-4908-bad7-ce82e1b1d340.1.0.0"),sQuery(id+"F0.wireOp",EDGE,"7093700b-8509-4908-bad7-ce82e1b1d340.1.0.2"),sQuery(id+"F0.wireOp",EDGE,"7093700b-8509-4908-bad7-ce82e1b1d340.1.0.3"),sQuery(id+"F0.wireOp",EDGE,"7093700b-8509-4908-bad7-ce82e1b1d340.1.0.5"),sQuery(id+"F0.wireOp",EDGE,"7093700b-8509-4908-bad7-ce82e1b1d340.1.0.6"),sQuery(id+"F0.wireOp",EDGE,"7093700b-8509-4908-bad7-ce82e1b1d340.1.0.7"),sQuery(id+"F0.wireOp",EDGE,"7093700b-8509-4908-bad7-ce82e1b1d340.1.0.8"),sQuery(id+"F0.wireOp",EDGE,"7093700b-8509-4908-bad7-ce82e1b1d340.1.0.9"),sQuery(id+"F0.wireOp",EDGE,"7093700b-8509-4908-bad7-ce82e1b1d340.1.0.12"),sQuery(id+"F0.wireOp",EDGE,"7093700b-8509-4908-bad7-ce82e1b1d340.1.0.13"),sQuery(id+"F0.wireOp",EDGE,"7093700b-8509-4908-bad7-ce82e1b1d340.1.0.14"),sQuery(id+"F0.wireOp",EDGE,"7093700b-8509-4908-bad7-ce82e1b1d340.1.0.15"),sQuery(id+"F0.wireOp",EDGE,"7093700b-8509-4908-bad7-ce82e1b1d340.1.0.16"),sQuery(id+"F0.wireOp",EDGE,"7093700b-8509-4908-bad7-ce82e1b1d340.1.0.17"),sQuery(id+"F0.wireOp",EDGE,"7093700b-8509-4908-bad7-ce82e1b1d340.1.0.18"),sQuery(id+"F0.wireOp",EDGE,"7093700b-8509-4908-bad7-ce82e1b1d340.1.0.19"),sQuery(id+"F0.wireOp",EDGE,"7093700b-8509-4908-bad7-ce82e1b1d340.1.0.20"),sQuery(id+"F0.wireOp",EDGE,"7093700b-8509-4908-bad7-ce82e1b1d340.1.0.21"),sQuery(id+"F0.wireOp",EDGE,"7093700b-8509-4908-bad7-ce82e1b1d340.2.0.0"),sQuery(id+"F0.wireOp",EDGE,"7093700b-8509-4908-bad7-ce82e1b1d340.2.0.2"),sQuery(id+"F0.wireOp",EDGE,"7093700b-8509-4908-bad7-ce82e1b1d340.2.0.3"),sQuery(id+"F0.wireOp",EDGE,"7093700b-8509-4908-bad7-ce82e1b1d340.2.0.5"),sQuery(id+"F0.wireOp",EDGE,"7093700b-8509-4908-bad7-ce82e1b1d340.2.0.6"),sQuery(id+"F0.wireOp",EDGE,"7093700b-8509-4908-bad7-ce82e1b1d340.2.0.7"),sQuery(id+"F0.wireOp",EDGE,"7093700b-8509-4908-bad7-ce82e1b1d340.2.0.8"),sQuery(id+"F0.wireOp",EDGE,"7093700b-8509-4908-bad7-ce82e1b1d340.2.0.9"),sQuery(id+"F0.wireOp",EDGE,"7093700b-8509-4908-bad7-ce82e1b1d340.2.0.12"),sQuery(id+"F0.wireOp",EDGE,"7093700b-8509-4908-bad7-ce82e1b1d340.2.0.13"),sQuery(id+"F0.wireOp",EDGE,"7093700b-8509-4908-bad7-ce82e1b1d340.2.0.14"),sQuery(id+"F0.wireOp",EDGE,"7093700b-8509-4908-bad7-ce82e1b1d340.2.0.15"),sQuery(id+"F0.wireOp",EDGE,"7093700b-8509-4908-bad7-ce82e1b1d340.2.0.16"),sQuery(id+"F0.wireOp",EDGE,"7093700b-8509-4908-bad7-ce82e1b1d340.2.0.17"),sQuery(id+"F0.wireOp",EDGE,"7093700b-8509-4908-bad7-ce82e1b1d340.2.0.18"),sQuery(id+"F0.wireOp",EDGE,"7093700b-8509-4908-bad7-ce82e1b1d340.2.0.19"),sQuery(id+"F0.wireOp",EDGE,"7093700b-8509-4908-bad7-ce82e1b1d340.2.0.20"),sQuery(id+"F0.wireOp",EDGE,"7093700b-8509-4908-bad7-ce82e1b1d340.2.0.21"),sQuery(id+"F0.wireOp",EDGE,"c973f7c2-3bf7-4545-afce-7af64f458de9.1.0.0"),sQuery(id+"F0.wireOp",EDGE,"c973f7c2-3bf7-4545-afce-7af64f458de9.1.0.1"),sQuery(id+"F0.wireOp",EDGE,"c973f7c2-3bf7-4545-afce-7af64f458de9.1.0.2"),sQuery(id+"F0.wireOp",EDGE,"c973f7c2-3bf7-4545-afce-7af64f458de9.1.0.4"),sQuery(id+"F0.wireOp",EDGE,"c973f7c2-3bf7-4545-afce-7af64f458de9.1.0.6"),sQuery(id+"F0.wireOp",EDGE,"c973f7c2-3bf7-4545-afce-7af64f458de9.1.0.7"),sQuery(id+"F0.wireOp",EDGE,"c973f7c2-3bf7-4545-afce-7af64f458de9.1.0.9"),sQuery(id+"F0.wireOp",EDGE,"c973f7c2-3bf7-4545-afce-7af64f458de9.1.0.10"),sQuery(id+"F0.wireOp",EDGE,"c973f7c2-3bf7-4545-afce-7af64f458de9.1.0.12"),sQuery(id+"F0.wireOp",EDGE,"c973f7c2-3bf7-4545-afce-7af64f458de9.1.0.14"),sQuery(id+"F0.wireOp",EDGE,"c973f7c2-3bf7-4545-afce-7af64f458de9.1.0.16"),sQuery(id+"F0.wireOp",EDGE,"c973f7c2-3bf7-4545-afce-7af64f458de9.1.0.18"),sQuery(id+"F0.wireOp",EDGE,"c973f7c2-3bf7-4545-afce-7af64f458de9.1.0.19"),sQuery(id+"F0.wireOp",EDGE,"c973f7c2-3bf7-4545-afce-7af64f458de9.1.0.20"),sQuery(id+"F0.wireOp",EDGE,"c973f7c2-3bf7-4545-afce-7af64f458de9.1.0.26"),sQuery(id+"F0.wireOp",EDGE,"c973f7c2-3bf7-4545-afce-7af64f458de9.1.0.28"),sQuery(id+"F0.wireOp",EDGE,"c973f7c2-3bf7-4545-afce-7af64f458de9.1.0.29"),sQuery(id+"F0.wireOp",EDGE,"c973f7c2-3bf7-4545-afce-7af64f458de9.1.0.30"),sQuery(id+"F0.wireOp",EDGE,"c973f7c2-3bf7-4545-afce-7af64f458de9.2.0.0"),sQuery(id+"F0.wireOp",EDGE,"c973f7c2-3bf7-4545-afce-7af64f458de9.2.0.1"),sQuery(id+"F0.wireOp",EDGE,"c973f7c2-3bf7-4545-afce-7af64f458de9.2.0.2"),sQuery(id+"F0.wireOp",EDGE,"c973f7c2-3bf7-4545-afce-7af64f458de9.2.0.4"),sQuery(id+"F0.wireOp",EDGE,"c973f7c2-3bf7-4545-afce-7af64f458de9.2.0.6"),sQuery(id+"F0.wireOp",EDGE,"c973f7c2-3bf7-4545-afce-7af64f458de9.2.0.7"),sQuery(id+"F0.wireOp",EDGE,"c973f7c2-3bf7-4545-afce-7af64f458de9.2.0.9"),sQuery(id+"F0.wireOp",EDGE,"c973f7c2-3bf7-4545-afce-7af64f458de9.2.0.10"),sQuery(id+"F0.wireOp",EDGE,"c973f7c2-3bf7-4545-afce-7af64f458de9.2.0.12"),sQuery(id+"F0.wireOp",EDGE,"c973f7c2-3bf7-4545-afce-7af64f458de9.2.0.14"),sQuery(id+"F0.wireOp",EDGE,"c973f7c2-3bf7-4545-afce-7af64f458de9.2.0.16"),sQuery(id+"F0.wireOp",EDGE,"c973f7c2-3bf7-4545-afce-7af64f458de9.2.0.18"),sQuery(id+"F0.wireOp",EDGE,"c973f7c2-3bf7-4545-afce-7af64f458de9.2.0.19"),sQuery(id+"F0.wireOp",EDGE,"c973f7c2-3bf7-4545-afce-7af64f458de9.2.0.20"),sQuery(id+"F0.wireOp",EDGE,"c973f7c2-3bf7-4545-afce-7af64f458de9.2.0.26"),sQuery(id+"F0.wireOp",EDGE,"c973f7c2-3bf7-4545-afce-7af64f458de9.2.0.28"),sQuery(id+"F0.wireOp",EDGE,"c973f7c2-3bf7-4545-afce-7af64f458de9.2.0.29"),sQuery(id+"F0.wireOp",EDGE,"c973f7c2-3bf7-4545-afce-7af64f458de9.2.0.30")])],"isStart":false});
            extrude(context, id + "F3", {"entities" : qUnion([Q0]), "operationType" : NewBodyOperationType.ADD, "depth" : 5 * mm});
        }
        {
            var Q0;
            Q0=makeQuery(id+"F3.opExtrude","CAP_FACE",FACE,{"disambiguationData":[OSD([sQuery(id+"F0.wireOp",EDGE,"E0.bottom"),sQuery(id+"F0.wireOp",EDGE,"E0.top"),sQuery(id+"F0.wireOp",EDGE,"E0.left"),sQuery(id+"F0.wireOp",EDGE,"E0.right"),sQuery(id+"F0.wireOp",EDGE,"E3"),sQuery(id+"F0.wireOp",EDGE,"E4"),sQuery(id+"F0.wireOp",EDGE,"E5"),sQuery(id+"F0.wireOp",EDGE,"E8"),sQuery(id+"F0.wireOp",EDGE,"E9"),sQuery(id+"F0.wireOp",EDGE,"E10"),sQuery(id+"F0.wireOp",EDGE,"E11"),sQuery(id+"F0.wireOp",EDGE,"E12"),sQuery(id+"F0.wireOp",EDGE,"E13"),sQuery(id+"F0.wireOp",EDGE,"E14"),sQuery(id+"F0.wireOp",EDGE,"E15.bottom"),sQuery(id+"F0.wireOp",EDGE,"E15.top"),sQuery(id+"F0.wireOp",EDGE,"E15.left"),sQuery(id+"F0.wireOp",EDGE,"E15.right"),sQuery(id+"F0.wireOp",EDGE,"E16"),sQuery(id+"F0.wireOp",EDGE,"E17"),sQuery(id+"F0.wireOp",EDGE,"E19.bottom"),sQuery(id+"F0.wireOp",EDGE,"E19.top"),sQuery(id+"F0.wireOp",EDGE,"E19.left"),sQuery(id+"F0.wireOp",EDGE,"E19.right"),sQuery(id+"F0.wireOp",EDGE,"E21.bottom"),sQuery(id+"F0.wireOp",EDGE,"E21.top"),sQuery(id+"F0.wireOp",EDGE,"E22.left"),sQuery(id+"F0.wireOp",EDGE,"E22.right"),sQuery(id+"F0.wireOp",EDGE,"E23.left"),sQuery(id+"F0.wireOp",EDGE,"E23.right"),sQuery(id+"F0.wireOp",EDGE,"E24.trimOffspring"),sQuery(id+"F0.wireOp",EDGE,"E25.trimOffspring"),sQuery(id+"F0.wireOp",EDGE,"E26.trimOffspring"),sQuery(id+"F0.wireOp",EDGE,"E27.trimOffspring"),sQuery(id+"F0.wireOp",EDGE,"E28.trimOffspring"),sQuery(id+"F0.wireOp",EDGE,"E29.trimOffspring"),sQuery(id+"F0.wireOp",EDGE,"E30.trimOffspring"),sQuery(id+"F0.wireOp",EDGE,"E31.trimOffspring"),sQuery(id+"F0.wireOp",EDGE,"E20.bottom"),sQuery(id+"F0.wireOp",EDGE,"E20.top"),sQuery(id+"F0.wireOp",EDGE,"E20.left"),sQuery(id+"F0.wireOp",EDGE,"E20.right"),sQuery(id+"F0.wireOp",EDGE,"E33.bottom"),sQuery(id+"F0.wireOp",EDGE,"E33.top"),sQuery(id+"F0.wireOp",EDGE,"E34.left"),sQuery(id+"F0.wireOp",EDGE,"E34.right"),sQuery(id+"F0.wireOp",EDGE,"E35.left"),sQuery(id+"F0.wireOp",EDGE,"E35.right"),sQuery(id+"F0.wireOp",EDGE,"E36.trimOffspring"),sQuery(id+"F0.wireOp",EDGE,"E37.trimOffspring"),sQuery(id+"F0.wireOp",EDGE,"E38.trimOffspring"),sQuery(id+"F0.wireOp",EDGE,"E39.trimOffspring"),sQuery(id+"F0.wireOp",EDGE,"E40.trimOffspring"),sQuery(id+"F0.wireOp",EDGE,"E41.trimOffspring"),sQuery(id+"F0.wireOp",EDGE,"E42.trimOffspring"),sQuery(id+"F0.wireOp",EDGE,"E43.trimOffspring"),sQuery(id+"F0.wireOp",EDGE,"E44.bottom"),sQuery(id+"F0.wireOp",EDGE,"E44.top"),sQuery(id+"F0.wireOp",EDGE,"E44.left"),sQuery(id+"F0.wireOp",EDGE,"E44.right"),sQuery(id+"F0.wireOp",EDGE,"E45.bottom"),sQuery(id+"F0.wireOp",EDGE,"E45.top"),sQuery(id+"F0.wireOp",EDGE,"E45.left"),sQuery(id+"F0.wireOp",EDGE,"E45.right"),sQuery(id+"F0.wireOp",EDGE,"7093700b-8509-4908-bad7-ce82e1b1d340.1.0.0"),sQuery(id+"F0.wireOp",EDGE,"7093700b-8509-4908-bad7-ce82e1b1d340.1.0.2"),sQuery(id+"F0.wireOp",EDGE,"7093700b-8509-4908-bad7-ce82e1b1d340.1.0.3"),sQuery(id+"F0.wireOp",EDGE,"7093700b-8509-4908-bad7-ce82e1b1d340.1.0.5"),sQuery(id+"F0.wireOp",EDGE,"7093700b-8509-4908-bad7-ce82e1b1d340.1.0.6"),sQuery(id+"F0.wireOp",EDGE,"7093700b-8509-4908-bad7-ce82e1b1d340.1.0.7"),sQuery(id+"F0.wireOp",EDGE,"7093700b-8509-4908-bad7-ce82e1b1d340.1.0.8"),sQuery(id+"F0.wireOp",EDGE,"7093700b-8509-4908-bad7-ce82e1b1d340.1.0.9"),sQuery(id+"F0.wireOp",EDGE,"7093700b-8509-4908-bad7-ce82e1b1d340.1.0.12"),sQuery(id+"F0.wireOp",EDGE,"7093700b-8509-4908-bad7-ce82e1b1d340.1.0.13"),sQuery(id+"F0.wireOp",EDGE,"7093700b-8509-4908-bad7-ce82e1b1d340.1.0.14"),sQuery(id+"F0.wireOp",EDGE,"7093700b-8509-4908-bad7-ce82e1b1d340.1.0.15"),sQuery(id+"F0.wireOp",EDGE,"7093700b-8509-4908-bad7-ce82e1b1d340.1.0.16"),sQuery(id+"F0.wireOp",EDGE,"7093700b-8509-4908-bad7-ce82e1b1d340.1.0.17"),sQuery(id+"F0.wireOp",EDGE,"7093700b-8509-4908-bad7-ce82e1b1d340.1.0.18"),sQuery(id+"F0.wireOp",EDGE,"7093700b-8509-4908-bad7-ce82e1b1d340.1.0.19"),sQuery(id+"F0.wireOp",EDGE,"7093700b-8509-4908-bad7-ce82e1b1d340.1.0.20"),sQuery(id+"F0.wireOp",EDGE,"7093700b-8509-4908-bad7-ce82e1b1d340.1.0.21"),sQuery(id+"F0.wireOp",EDGE,"7093700b-8509-4908-bad7-ce82e1b1d340.2.0.0"),sQuery(id+"F0.wireOp",EDGE,"7093700b-8509-4908-bad7-ce82e1b1d340.2.0.2"),sQuery(id+"F0.wireOp",EDGE,"7093700b-8509-4908-bad7-ce82e1b1d340.2.0.3"),sQuery(id+"F0.wireOp",EDGE,"7093700b-8509-4908-bad7-ce82e1b1d340.2.0.5"),sQuery(id+"F0.wireOp",EDGE,"7093700b-8509-4908-bad7-ce82e1b1d340.2.0.6"),sQuery(id+"F0.wireOp",EDGE,"7093700b-8509-4908-bad7-ce82e1b1d340.2.0.7"),sQuery(id+"F0.wireOp",EDGE,"7093700b-8509-4908-bad7-ce82e1b1d340.2.0.8"),sQuery(id+"F0.wireOp",EDGE,"7093700b-8509-4908-bad7-ce82e1b1d340.2.0.9"),sQuery(id+"F0.wireOp",EDGE,"7093700b-8509-4908-bad7-ce82e1b1d340.2.0.12"),sQuery(id+"F0.wireOp",EDGE,"7093700b-8509-4908-bad7-ce82e1b1d340.2.0.13"),sQuery(id+"F0.wireOp",EDGE,"7093700b-8509-4908-bad7-ce82e1b1d340.2.0.14"),sQuery(id+"F0.wireOp",EDGE,"7093700b-8509-4908-bad7-ce82e1b1d340.2.0.15"),sQuery(id+"F0.wireOp",EDGE,"7093700b-8509-4908-bad7-ce82e1b1d340.2.0.16"),sQuery(id+"F0.wireOp",EDGE,"7093700b-8509-4908-bad7-ce82e1b1d340.2.0.17"),sQuery(id+"F0.wireOp",EDGE,"7093700b-8509-4908-bad7-ce82e1b1d340.2.0.18"),sQuery(id+"F0.wireOp",EDGE,"7093700b-8509-4908-bad7-ce82e1b1d340.2.0.19"),sQuery(id+"F0.wireOp",EDGE,"7093700b-8509-4908-bad7-ce82e1b1d340.2.0.20"),sQuery(id+"F0.wireOp",EDGE,"7093700b-8509-4908-bad7-ce82e1b1d340.2.0.21"),sQuery(id+"F0.wireOp",EDGE,"c973f7c2-3bf7-4545-afce-7af64f458de9.1.0.0"),sQuery(id+"F0.wireOp",EDGE,"c973f7c2-3bf7-4545-afce-7af64f458de9.1.0.1"),sQuery(id+"F0.wireOp",EDGE,"c973f7c2-3bf7-4545-afce-7af64f458de9.1.0.2"),sQuery(id+"F0.wireOp",EDGE,"c973f7c2-3bf7-4545-afce-7af64f458de9.1.0.4"),sQuery(id+"F0.wireOp",EDGE,"c973f7c2-3bf7-4545-afce-7af64f458de9.1.0.6"),sQuery(id+"F0.wireOp",EDGE,"c973f7c2-3bf7-4545-afce-7af64f458de9.1.0.7"),sQuery(id+"F0.wireOp",EDGE,"c973f7c2-3bf7-4545-afce-7af64f458de9.1.0.9"),sQuery(id+"F0.wireOp",EDGE,"c973f7c2-3bf7-4545-afce-7af64f458de9.1.0.10"),sQuery(id+"F0.wireOp",EDGE,"c973f7c2-3bf7-4545-afce-7af64f458de9.1.0.12"),sQuery(id+"F0.wireOp",EDGE,"c973f7c2-3bf7-4545-afce-7af64f458de9.1.0.14"),sQuery(id+"F0.wireOp",EDGE,"c973f7c2-3bf7-4545-afce-7af64f458de9.1.0.16"),sQuery(id+"F0.wireOp",EDGE,"c973f7c2-3bf7-4545-afce-7af64f458de9.1.0.18"),sQuery(id+"F0.wireOp",EDGE,"c973f7c2-3bf7-4545-afce-7af64f458de9.1.0.19"),sQuery(id+"F0.wireOp",EDGE,"c973f7c2-3bf7-4545-afce-7af64f458de9.1.0.20"),sQuery(id+"F0.wireOp",EDGE,"c973f7c2-3bf7-4545-afce-7af64f458de9.1.0.26"),sQuery(id+"F0.wireOp",EDGE,"c973f7c2-3bf7-4545-afce-7af64f458de9.1.0.28"),sQuery(id+"F0.wireOp",EDGE,"c973f7c2-3bf7-4545-afce-7af64f458de9.1.0.29"),sQuery(id+"F0.wireOp",EDGE,"c973f7c2-3bf7-4545-afce-7af64f458de9.1.0.30"),sQuery(id+"F0.wireOp",EDGE,"c973f7c2-3bf7-4545-afce-7af64f458de9.2.0.0"),sQuery(id+"F0.wireOp",EDGE,"c973f7c2-3bf7-4545-afce-7af64f458de9.2.0.1"),sQuery(id+"F0.wireOp",EDGE,"c973f7c2-3bf7-4545-afce-7af64f458de9.2.0.2"),sQuery(id+"F0.wireOp",EDGE,"c973f7c2-3bf7-4545-afce-7af64f458de9.2.0.4"),sQuery(id+"F0.wireOp",EDGE,"c973f7c2-3bf7-4545-afce-7af64f458de9.2.0.6"),sQuery(id+"F0.wireOp",EDGE,"c973f7c2-3bf7-4545-afce-7af64f458de9.2.0.7"),sQuery(id+"F0.wireOp",EDGE,"c973f7c2-3bf7-4545-afce-7af64f458de9.2.0.9"),sQuery(id+"F0.wireOp",EDGE,"c973f7c2-3bf7-4545-afce-7af64f458de9.2.0.10"),sQuery(id+"F0.wireOp",EDGE,"c973f7c2-3bf7-4545-afce-7af64f458de9.2.0.12"),sQuery(id+"F0.wireOp",EDGE,"c973f7c2-3bf7-4545-afce-7af64f458de9.2.0.14"),sQuery(id+"F0.wireOp",EDGE,"c973f7c2-3bf7-4545-afce-7af64f458de9.2.0.16"),sQuery(id+"F0.wireOp",EDGE,"c973f7c2-3bf7-4545-afce-7af64f458de9.2.0.18"),sQuery(id+"F0.wireOp",EDGE,"c973f7c2-3bf7-4545-afce-7af64f458de9.2.0.19"),sQuery(id+"F0.wireOp",EDGE,"c973f7c2-3bf7-4545-afce-7af64f458de9.2.0.20"),sQuery(id+"F0.wireOp",EDGE,"c973f7c2-3bf7-4545-afce-7af64f458de9.2.0.26"),sQuery(id+"F0.wireOp",EDGE,"c973f7c2-3bf7-4545-afce-7af64f458de9.2.0.28"),sQuery(id+"F0.wireOp",EDGE,"c973f7c2-3bf7-4545-afce-7af64f458de9.2.0.29"),sQuery(id+"F0.wireOp",EDGE,"c973f7c2-3bf7-4545-afce-7af64f458de9.2.0.30")])],"isStart":false});
            var sketch = newSketch(context, id + "F4", { "sketchPlane" : qUnion([Q0])});
            skPoint(sketch, "E93.0", {"position": v(-109.5, 1.96) * mm});
            skLineSegment(sketch, "E94.bottom", {"start": v(-100.5, -7.04) * mm, "end": v(-118.5, -7.04) * mm});
            skLineSegment(sketch, "E94.top", {"start": v(-100.5, 10.96) * mm, "end": v(-118.5, 10.96) * mm});
            skLineSegment(sketch, "E94.left", {"start": v(-100.5, -7.04) * mm, "end": v(-100.5, 10.96) * mm});
            skLineSegment(sketch, "E94.right", {"start": v(-118.5, -7.04) * mm, "end": v(-118.5, 10.96) * mm});
            skPoint(sketch, "E95.0", {"position": v(-109.5, -21.04) * mm});
            skLineSegment(sketch, "E96.bottom", {"start": v(-100.5, -30.04) * mm, "end": v(-118.5, -30.04) * mm});
            skLineSegment(sketch, "E96.top", {"start": v(-100.5, -12.04) * mm, "end": v(-118.5, -12.04) * mm});
            skLineSegment(sketch, "E96.left", {"start": v(-100.5, -30.04) * mm, "end": v(-100.5, -12.04) * mm});
            skLineSegment(sketch, "E96.right", {"start": v(-118.5, -30.04) * mm, "end": v(-118.5, -12.04) * mm});
            skPoint(sketch, "E97.0", {"position": v(-119.5, -21.04) * mm});
            skPoint(sketch, "E97.1", {"position": v(-119.5, 1.96) * mm});
            skLineSegment(sketch, "E98.bottom", {"start": v(-118.5, -3.04) * mm, "end": v(-120.5, -3.04) * mm});
            skLineSegment(sketch, "E98.top", {"start": v(-118.5, 6.96) * mm, "end": v(-120.5, 6.96) * mm});
            skLineSegment(sketch, "E98.left", {"start": v(-118.5, -3.04) * mm, "end": v(-118.5, 6.96) * mm});
            skLineSegment(sketch, "E98.right", {"start": v(-120.5, -3.04) * mm, "end": v(-120.5, 6.96) * mm});
            skPoint(sketch, "E99.0", {"position": v(-99.5, 1.96) * mm});
            skLineSegment(sketch, "E100.bottom", {"start": v(-100.5, -3.04) * mm, "end": v(-98.5, -3.04) * mm});
            skLineSegment(sketch, "E100.top", {"start": v(-100.5, 6.96) * mm, "end": v(-98.5, 6.96) * mm});
            skLineSegment(sketch, "E100.left", {"start": v(-100.5, -3.04) * mm, "end": v(-100.5, 6.96) * mm});
            skLineSegment(sketch, "E100.right", {"start": v(-98.5, -3.04) * mm, "end": v(-98.5, 6.96) * mm});
            skPoint(sketch, "E101.1.0.0", {"position": v(-72.5, 1.96) * mm});
            skPoint(sketch, "E101.1.0.1", {"position": v(-92.5, 1.96) * mm});
            skLineSegment(sketch, "E101.1.0.2", {"start": v(-73.5, -3.04) * mm, "end": v(-71.5, -3.04) * mm});
            skLineSegment(sketch, "E101.1.0.3", {"start": v(-73.5, 6.96) * mm, "end": v(-71.5, 6.96) * mm});
            skLineSegment(sketch, "E101.1.0.4", {"start": v(-91.5, -3.04) * mm, "end": v(-93.5, -3.04) * mm});
            skLineSegment(sketch, "E101.1.0.5", {"start": v(-73.5, 10.96) * mm, "end": v(-91.5, 10.96) * mm});
            skLineSegment(sketch, "E101.1.0.6", {"start": v(-73.5, -7.04) * mm, "end": v(-73.5, 10.96) * mm});
            skPoint(sketch, "E101.1.0.7", {"position": v(-82.5, 1.96) * mm});
            skLineSegment(sketch, "E101.1.0.8", {"start": v(-91.5, 6.96) * mm, "end": v(-93.5, 6.96) * mm});
            skLineSegment(sketch, "E101.1.0.9", {"start": v(-73.5, -7.04) * mm, "end": v(-91.5, -7.04) * mm});
            skLineSegment(sketch, "E101.1.0.10", {"start": v(-91.5, -7.04) * mm, "end": v(-91.5, 10.96) * mm});
            skLineSegment(sketch, "E101.1.0.11", {"start": v(-93.5, -3.04) * mm, "end": v(-93.5, 6.96) * mm});
            skLineSegment(sketch, "E101.1.0.12", {"start": v(-71.5, -3.04) * mm, "end": v(-71.5, 6.96) * mm});
            skPoint(sketch, "E101.1.0.13", {"position": v(-92.5, 1.96) * mm});
            skLineSegment(sketch, "E101.1.0.14", {"start": v(-73.5, -3.04) * mm, "end": v(-73.5, 6.96) * mm});
            skPoint(sketch, "E101.1.0.15", {"position": v(-72.5, 1.96) * mm});
            skLineSegment(sketch, "E101.1.0.16", {"start": v(-91.5, -3.04) * mm, "end": v(-91.5, 6.96) * mm});
            skPoint(sketch, "E101.1.0.17", {"position": v(-82.5, 1.96) * mm});
            skPoint(sketch, "E101.2.0.0", {"position": v(-45.5, 1.96) * mm});
            skPoint(sketch, "E101.2.0.1", {"position": v(-65.5, 1.96) * mm});
            skLineSegment(sketch, "E101.2.0.2", {"start": v(-46.5, -3.04) * mm, "end": v(-44.5, -3.04) * mm});
            skLineSegment(sketch, "E101.2.0.3", {"start": v(-46.5, 6.96) * mm, "end": v(-44.5, 6.96) * mm});
            skLineSegment(sketch, "E101.2.0.4", {"start": v(-64.5, -3.04) * mm, "end": v(-66.5, -3.04) * mm});
            skLineSegment(sketch, "E101.2.0.5", {"start": v(-46.5, 10.96) * mm, "end": v(-64.5, 10.96) * mm});
            skLineSegment(sketch, "E101.2.0.6", {"start": v(-46.5, -7.04) * mm, "end": v(-46.5, 10.96) * mm});
            skPoint(sketch, "E101.2.0.7", {"position": v(-55.5, 1.96) * mm});
            skLineSegment(sketch, "E101.2.0.8", {"start": v(-64.5, 6.96) * mm, "end": v(-66.5, 6.96) * mm});
            skLineSegment(sketch, "E101.2.0.9", {"start": v(-46.5, -7.04) * mm, "end": v(-64.5, -7.04) * mm});
            skLineSegment(sketch, "E101.2.0.10", {"start": v(-64.5, -7.04) * mm, "end": v(-64.5, 10.96) * mm});
            skLineSegment(sketch, "E101.2.0.11", {"start": v(-66.5, -3.04) * mm, "end": v(-66.5, 6.96) * mm});
            skLineSegment(sketch, "E101.2.0.12", {"start": v(-44.5, -3.04) * mm, "end": v(-44.5, 6.96) * mm});
            skPoint(sketch, "E101.2.0.13", {"position": v(-65.5, 1.96) * mm});
            skLineSegment(sketch, "E101.2.0.14", {"start": v(-46.5, -3.04) * mm, "end": v(-46.5, 6.96) * mm});
            skPoint(sketch, "E101.2.0.15", {"position": v(-45.5, 1.96) * mm});
            skLineSegment(sketch, "E101.2.0.16", {"start": v(-64.5, -3.04) * mm, "end": v(-64.5, 6.96) * mm});
            skPoint(sketch, "E101.2.0.17", {"position": v(-55.5, 1.96) * mm});
            skLineSegment(sketch, "E101.direction1", {"start": v(-118.5, -7.04) * mm, "end": v(-91.5, -7.04) * mm, "construction": true});
            skLineSegment(sketch, "E102.bottom", {"start": v(-118.5, -26.04) * mm, "end": v(-120.5, -26.04) * mm});
            skLineSegment(sketch, "E102.top", {"start": v(-118.5, -16.04) * mm, "end": v(-120.5, -16.04) * mm});
            skLineSegment(sketch, "E102.left", {"start": v(-118.5, -26.04) * mm, "end": v(-118.5, -16.04) * mm});
            skLineSegment(sketch, "E102.right", {"start": v(-120.5, -26.04) * mm, "end": v(-120.5, -16.04) * mm});
            skPoint(sketch, "E103.0", {"position": v(-99.5, -21.04) * mm});
            skLineSegment(sketch, "E104.bottom", {"start": v(-100.5, -16.04) * mm, "end": v(-98.5, -16.04) * mm});
            skLineSegment(sketch, "E104.top", {"start": v(-100.5, -26.04) * mm, "end": v(-98.5, -26.04) * mm});
            skLineSegment(sketch, "E104.left", {"start": v(-100.5, -16.04) * mm, "end": v(-100.5, -26.04) * mm});
            skLineSegment(sketch, "E104.right", {"start": v(-98.5, -16.04) * mm, "end": v(-98.5, -26.04) * mm});
            skPoint(sketch, "E105.1.0.0", {"position": v(-92.5, -21.04) * mm});
            skLineSegment(sketch, "E105.1.0.1", {"start": v(-71.5, -16.04) * mm, "end": v(-71.5, -26.04) * mm});
            skLineSegment(sketch, "E105.1.0.2", {"start": v(-73.5, -26.04) * mm, "end": v(-71.5, -26.04) * mm});
            skLineSegment(sketch, "E105.1.0.3", {"start": v(-73.5, -30.04) * mm, "end": v(-73.5, -12.04) * mm});
            skLineSegment(sketch, "E105.1.0.4", {"start": v(-91.5, -30.04) * mm, "end": v(-91.5, -12.04) * mm});
            skLineSegment(sketch, "E105.1.0.5", {"start": v(-91.5, -16.04) * mm, "end": v(-93.5, -16.04) * mm});
            skLineSegment(sketch, "E105.1.0.6", {"start": v(-91.5, -26.04) * mm, "end": v(-93.5, -26.04) * mm});
            skLineSegment(sketch, "E105.1.0.7", {"start": v(-73.5, -30.04) * mm, "end": v(-91.5, -30.04) * mm});
            skPoint(sketch, "E105.1.0.8", {"position": v(-72.5, -21.04) * mm});
            skLineSegment(sketch, "E105.1.0.9", {"start": v(-73.5, -12.04) * mm, "end": v(-91.5, -12.04) * mm});
            skLineSegment(sketch, "E105.1.0.10", {"start": v(-73.5, -16.04) * mm, "end": v(-71.5, -16.04) * mm});
            skPoint(sketch, "E105.1.0.11", {"position": v(-82.5, -21.04) * mm});
            skLineSegment(sketch, "E105.1.0.12", {"start": v(-93.5, -26.04) * mm, "end": v(-93.5, -16.04) * mm});
            skLineSegment(sketch, "E105.1.0.13", {"start": v(-73.5, -16.04) * mm, "end": v(-73.5, -26.04) * mm});
            skLineSegment(sketch, "E105.1.0.14", {"start": v(-91.5, -26.04) * mm, "end": v(-91.5, -16.04) * mm});
            skPoint(sketch, "E105.1.0.15", {"position": v(-82.5, -21.04) * mm});
            skPoint(sketch, "E105.1.0.16", {"position": v(-72.5, -21.04) * mm});
            skPoint(sketch, "E105.1.0.17", {"position": v(-92.5, -21.04) * mm});
            skPoint(sketch, "E105.2.0.0", {"position": v(-65.5, -21.04) * mm});
            skLineSegment(sketch, "E105.2.0.1", {"start": v(-44.5, -16.04) * mm, "end": v(-44.5, -26.04) * mm});
            skLineSegment(sketch, "E105.2.0.2", {"start": v(-46.5, -26.04) * mm, "end": v(-44.5, -26.04) * mm});
            skLineSegment(sketch, "E105.2.0.3", {"start": v(-46.5, -30.04) * mm, "end": v(-46.5, -12.04) * mm});
            skLineSegment(sketch, "E105.2.0.4", {"start": v(-64.5, -30.04) * mm, "end": v(-64.5, -12.04) * mm});
            skLineSegment(sketch, "E105.2.0.5", {"start": v(-64.5, -16.04) * mm, "end": v(-66.5, -16.04) * mm});
            skLineSegment(sketch, "E105.2.0.6", {"start": v(-64.5, -26.04) * mm, "end": v(-66.5, -26.04) * mm});
            skLineSegment(sketch, "E105.2.0.7", {"start": v(-46.5, -30.04) * mm, "end": v(-64.5, -30.04) * mm});
            skPoint(sketch, "E105.2.0.8", {"position": v(-45.5, -21.04) * mm});
            skLineSegment(sketch, "E105.2.0.9", {"start": v(-46.5, -12.04) * mm, "end": v(-64.5, -12.04) * mm});
            skLineSegment(sketch, "E105.2.0.10", {"start": v(-46.5, -16.04) * mm, "end": v(-44.5, -16.04) * mm});
            skPoint(sketch, "E105.2.0.11", {"position": v(-55.5, -21.04) * mm});
            skLineSegment(sketch, "E105.2.0.12", {"start": v(-66.5, -26.04) * mm, "end": v(-66.5, -16.04) * mm});
            skLineSegment(sketch, "E105.2.0.13", {"start": v(-46.5, -16.04) * mm, "end": v(-46.5, -26.04) * mm});
            skLineSegment(sketch, "E105.2.0.14", {"start": v(-64.5, -26.04) * mm, "end": v(-64.5, -16.04) * mm});
            skPoint(sketch, "E105.2.0.15", {"position": v(-55.5, -21.04) * mm});
            skPoint(sketch, "E105.2.0.16", {"position": v(-45.5, -21.04) * mm});
            skPoint(sketch, "E105.2.0.17", {"position": v(-65.5, -21.04) * mm});
            skLineSegment(sketch, "E105.direction1", {"start": v(-118.5, -30.04) * mm, "end": v(-91.5, -30.04) * mm, "construction": true});
            skPoint(sketch, "E106.0", {"position": v(-132, 1.96) * mm});
            skPoint(sketch, "E106.1", {"position": v(-132, -21.04) * mm});
            skLineSegment(sketch, "E107.bottom", {"start": v(-127, -3.04) * mm, "end": v(-137, -3.04) * mm});
            skLineSegment(sketch, "E107.top", {"start": v(-127, 6.96) * mm, "end": v(-137, 6.96) * mm});
            skLineSegment(sketch, "E107.left", {"start": v(-127, -3.04) * mm, "end": v(-127, 6.96) * mm});
            skLineSegment(sketch, "E107.right", {"start": v(-137, -3.04) * mm, "end": v(-137, 6.96) * mm});
            skLineSegment(sketch, "E108.bottom", {"start": v(-127, -26.04) * mm, "end": v(-137, -26.04) * mm});
            skLineSegment(sketch, "E108.top", {"start": v(-127, -16.04) * mm, "end": v(-137, -16.04) * mm});
            skLineSegment(sketch, "E108.left", {"start": v(-127, -26.04) * mm, "end": v(-127, -16.04) * mm});
            skLineSegment(sketch, "E108.right", {"start": v(-137, -26.04) * mm, "end": v(-137, -16.04) * mm});
            skSolve(sketch);
        }
        {
            var Q0;
            Q0=qSketchRegion(id+"F4",true);
            extrude(context, id + "F5", {"entities" : qUnion([Q0]), "operationType" : NewBodyOperationType.REMOVE, "oppositeDirection" : true, "depth" : 5 * mm});
        }
        {
            var Q0;
            Q0=qCreatedBy(makeId("Top.planeOp"),FACE);
            var sketch = newSketch(context, id + "F6", { "sketchPlane" : qUnion([Q0])});
            skLineSegment(sketch, "E109.bottom", {"start": v(-106.79, 77.03) * mm, "end": v(-126.79, 77.03) * mm});
            skLineSegment(sketch, "E109.top", {"start": v(-106.79, 97.03) * mm, "end": v(-126.79, 97.03) * mm});
            skLineSegment(sketch, "E109.left", {"start": v(-106.79, 77.03) * mm, "end": v(-106.79, 97.03) * mm});
            skLineSegment(sketch, "E109.right", {"start": v(-126.79, 77.03) * mm, "end": v(-126.79, 97.03) * mm});
            skPoint(sketch, "E109.middle", {"position": v(-116.79, 87.03) * mm});
            skLineSegment(sketch, "E110.bottom", {"start": v(-105.79, 82.03) * mm, "end": v(-107.79, 82.03) * mm});
            skLineSegment(sketch, "E110.top", {"start": v(-105.79, 92.03) * mm, "end": v(-107.79, 92.03) * mm});
            skLineSegment(sketch, "E110.left", {"start": v(-105.79, 82.03) * mm, "end": v(-105.79, 92.03) * mm});
            skLineSegment(sketch, "E110.right", {"start": v(-107.79, 82.03) * mm, "end": v(-107.79, 92.03) * mm});
            skPoint(sketch, "E110.middle", {"position": v(-106.79, 87.03) * mm});
            skLineSegment(sketch, "E111.bottom", {"start": v(-125.79, 82.03) * mm, "end": v(-127.79, 82.03) * mm});
            skLineSegment(sketch, "E111.top", {"start": v(-125.79, 92.03) * mm, "end": v(-127.79, 92.03) * mm});
            skLineSegment(sketch, "E111.left", {"start": v(-125.79, 82.03) * mm, "end": v(-125.79, 92.03) * mm});
            skLineSegment(sketch, "E111.right", {"start": v(-127.79, 82.03) * mm, "end": v(-127.79, 92.03) * mm});
            skPoint(sketch, "E111.middle", {"position": v(-126.79, 87.03) * mm});
            skLineSegment(sketch, "E112.bottom", {"start": v(-107.79, 78.03) * mm, "end": v(-125.79, 78.03) * mm});
            skLineSegment(sketch, "E112.top", {"start": v(-107.79, 96.03) * mm, "end": v(-125.79, 96.03) * mm});
            skLineSegment(sketch, "E112.left", {"start": v(-107.79, 78.03) * mm, "end": v(-107.79, 96.03) * mm});
            skLineSegment(sketch, "E112.right", {"start": v(-125.79, 78.03) * mm, "end": v(-125.79, 96.03) * mm});
            skLineSegment(sketch, "E113.bottom", {"start": v(-107.79, 86.53) * mm, "end": v(-125.79, 86.53) * mm});
            skLineSegment(sketch, "E113.top", {"start": v(-107.79, 87.53) * mm, "end": v(-125.79, 87.53) * mm});
            skLineSegment(sketch, "E113.left", {"start": v(-107.79, 86.53) * mm, "end": v(-107.79, 87.53) * mm});
            skLineSegment(sketch, "E113.right", {"start": v(-125.79, 86.53) * mm, "end": v(-125.79, 87.53) * mm});
            skLineSegment(sketch, "E114.bottom", {"start": v(-115.79, 85.78) * mm, "end": v(-117.79, 85.78) * mm, "construction": true});
            skLineSegment(sketch, "E114.top", {"start": v(-115.79, 88.28) * mm, "end": v(-117.79, 88.28) * mm, "construction": true});
            skLineSegment(sketch, "E114.left", {"start": v(-115.79, 85.78) * mm, "end": v(-115.79, 88.28) * mm, "construction": true});
            skLineSegment(sketch, "E114.right", {"start": v(-117.79, 85.78) * mm, "end": v(-117.79, 88.28) * mm, "construction": true});
            skLineSegment(sketch, "E115.bottom", {"start": v(-110.82, 38.4) * mm, "end": v(-132.62, 38.4) * mm});
            skLineSegment(sketch, "E115.top", {"start": v(-110.82, 60.2) * mm, "end": v(-132.62, 60.2) * mm});
            skLineSegment(sketch, "E115.left", {"start": v(-110.82, 38.4) * mm, "end": v(-110.82, 60.2) * mm});
            skLineSegment(sketch, "E115.right", {"start": v(-132.62, 38.4) * mm, "end": v(-132.62, 60.2) * mm});
            skPoint(sketch, "E115.middle", {"position": v(-121.72, 49.3) * mm});
            skLineSegment(sketch, "E116.bottom", {"start": v(-110.82, 44.4) * mm, "end": v(-112.62, 44.4) * mm});
            skLineSegment(sketch, "E116.top", {"start": v(-110.82, 54.2) * mm, "end": v(-112.62, 54.2) * mm});
            skLineSegment(sketch, "E116.left", {"start": v(-110.82, 44.4) * mm, "end": v(-110.82, 54.2) * mm});
            skLineSegment(sketch, "E116.right", {"start": v(-112.62, 44.4) * mm, "end": v(-112.62, 54.2) * mm});
            skPoint(sketch, "E116.middle", {"position": v(-111.72, 49.3) * mm});
            skLineSegment(sketch, "E117.bottom", {"start": v(-130.82, 44.4) * mm, "end": v(-132.62, 44.4) * mm});
            skLineSegment(sketch, "E117.top", {"start": v(-130.82, 54.2) * mm, "end": v(-132.62, 54.2) * mm});
            skLineSegment(sketch, "E117.left", {"start": v(-130.82, 44.4) * mm, "end": v(-130.82, 54.2) * mm});
            skLineSegment(sketch, "E117.right", {"start": v(-132.62, 44.4) * mm, "end": v(-132.62, 54.2) * mm});
            skPoint(sketch, "E117.middle", {"position": v(-131.72, 49.3) * mm});
            skLineSegment(sketch, "E118.bottom", {"start": v(-112.62, 40.2) * mm, "end": v(-130.82, 40.2) * mm});
            skLineSegment(sketch, "E118.top", {"start": v(-112.62, 58.4) * mm, "end": v(-130.82, 58.4) * mm});
            skLineSegment(sketch, "E118.left", {"start": v(-112.62, 40.2) * mm, "end": v(-112.62, 58.4) * mm});
            skLineSegment(sketch, "E118.right", {"start": v(-130.82, 40.2) * mm, "end": v(-130.82, 58.4) * mm});
            skSolve(sketch);
        }
        {
            var Q0;
            {var subQ11=sQuery(id+"F6.wireOp",EDGE,"E115.bottom");Q0=makeQuery(id+"F6.imprint","IMPRINT",FACE,{"disambiguationData":[TD([[makeQuery(id+"F6.imprint","IMPRINT",EDGE,{"derivedFrom":subQ11}),-1.0]])]});}
            var Q1;
            {var subQ5=sQuery(id+"F6.wireOp",EDGE,"E116.right");Q1=makeQuery(id+"F6.imprint","IMPRINT",FACE,{"disambiguationData":[TD([[makeQuery(id+"F6.imprint","IMPRINT",EDGE,{"derivedFrom":subQ5}),-1.0]])]});}
            var Q2;
            {var subQ5=sQuery(id+"F6.wireOp",EDGE,"E117.left");Q2=makeQuery(id+"F6.imprint","IMPRINT",FACE,{"disambiguationData":[TD([[makeQuery(id+"F6.imprint","IMPRINT",EDGE,{"derivedFrom":subQ5}),1.0]])]});}
            var Q3;
            {var subQ0=sQuery(id+"F6.wireOp",EDGE,"E117.bottom");Q3=makeQuery(id+"F6.imprint","IMPRINT",FACE,{"disambiguationData":[TD([[makeQuery(id+"F6.imprint","IMPRINT",EDGE,{"derivedFrom":subQ0}),-1.0]])]});}
            var Q4;
            {var subQ2=sQuery(id+"F6.wireOp",EDGE,"E115.top");Q4=makeQuery(id+"F6.imprint","IMPRINT",FACE,{"disambiguationData":[TD([[makeQuery(id+"F6.imprint","IMPRINT",EDGE,{"derivedFrom":subQ2}),1.0]])]});}
            var Q5;
            {var subQ0=sQuery(id+"F6.wireOp",EDGE,"E116.bottom");Q5=makeQuery(id+"F6.imprint","IMPRINT",FACE,{"disambiguationData":[TD([[makeQuery(id+"F6.imprint","IMPRINT",EDGE,{"derivedFrom":subQ0}),-1.0]])]});}
            extrude(context, id + "F7", {"entities" : qUnion([Q0, Q1, Q2, Q3, Q4, Q5]), "depth" : 1 * mm});
        }
        {
            var Q0;
            {var subQ5=sQuery(id+"F6.wireOp",EDGE,"E117.right");Q0=makeQuery(id+"F6.imprint","IMPRINT",FACE,{"disambiguationData":[TD([[makeQuery(id+"F6.imprint","IMPRINT",EDGE,{"derivedFrom":subQ5}),-1.0]])]});}
            var Q1;
            {var subQ5=sQuery(id+"F6.wireOp",EDGE,"E117.left");Q1=makeQuery(id+"F6.imprint","IMPRINT",FACE,{"disambiguationData":[TD([[makeQuery(id+"F6.imprint","IMPRINT",EDGE,{"derivedFrom":subQ5}),1.0]])]});}
            var Q2;
            {var subQ5=sQuery(id+"F6.wireOp",EDGE,"E116.right");Q2=makeQuery(id+"F6.imprint","IMPRINT",FACE,{"disambiguationData":[TD([[makeQuery(id+"F6.imprint","IMPRINT",EDGE,{"derivedFrom":subQ5}),-1.0]])]});}
            var Q3;
            {var subQ5=sQuery(id+"F6.wireOp",EDGE,"E116.left");Q3=makeQuery(id+"F6.imprint","IMPRINT",FACE,{"disambiguationData":[TD([[makeQuery(id+"F6.imprint","IMPRINT",EDGE,{"derivedFrom":subQ5}),1.0]])]});}
            extrude(context, id + "F8", {"entities" : qUnion([Q0, Q1, Q2, Q3]), "operationType" : NewBodyOperationType.ADD, "oppositeDirection" : true, "depth" : 4 * mm});
        }
        {
            var Q0;
            Q0=makeQuery(id+"F7.opExtrude","CAP_FACE",FACE,{"disambiguationData":[OSD([sQuery(id+"F6.wireOp",EDGE,"E115.bottom"),sQuery(id+"F6.wireOp",EDGE,"E115.top"),sQuery(id+"F6.wireOp",EDGE,"E115.left"),sQuery(id+"F6.wireOp",EDGE,"E115.right"),sQuery(id+"F6.wireOp",EDGE,"E116.left"),sQuery(id+"F6.wireOp",EDGE,"E117.right"),sQuery(id+"F6.wireOp",EDGE,"E118.bottom"),sQuery(id+"F6.wireOp",EDGE,"E118.top"),sQuery(id+"F6.wireOp",EDGE,"E118.left"),sQuery(id+"F6.wireOp",EDGE,"E118.right")])],"isStart":false});
            var sketch = newSketch(context, id + "F9", { "sketchPlane" : qUnion([Q0])});
            skPoint(sketch, "E119.0", {"position": v(-121.72, 49.3) * mm});
            skLineSegment(sketch, "E120.bottom", {"start": v(-112.62, 40.2) * mm, "end": v(-130.82, 40.2) * mm});
            skLineSegment(sketch, "E120.top", {"start": v(-112.62, 58.4) * mm, "end": v(-130.82, 58.4) * mm});
            skLineSegment(sketch, "E120.left", {"start": v(-112.62, 40.2) * mm, "end": v(-112.62, 58.4) * mm});
            skLineSegment(sketch, "E120.right", {"start": v(-130.82, 40.2) * mm, "end": v(-130.82, 58.4) * mm});
            skLineSegment(sketch, "E121.0", {"start": v(-131.82, 39.2) * mm, "end": v(-131.82, 59.4) * mm});
            skLineSegment(sketch, "E121.1", {"start": v(-111.62, 39.2) * mm, "end": v(-131.82, 39.2) * mm});
            skLineSegment(sketch, "E121.2", {"start": v(-111.62, 39.2) * mm, "end": v(-111.62, 59.4) * mm});
            skLineSegment(sketch, "E121.3", {"start": v(-111.62, 59.4) * mm, "end": v(-131.82, 59.4) * mm});
            skSolve(sketch);
        }
        {
            var Q0;
            Q0=makeQuery(id+"F9.imprint","IMPRINT",FACE,{"disambiguationData":[TD([[makeQuery(id+"F9.imprint","IMPRINT",EDGE,{"derivedFrom":sQuery(id+"F9.wireOp",EDGE,"E120.bottom")}),1.0]])]});
            extrude(context, id + "F10", {"entities" : qUnion([Q0]), "operationType" : NewBodyOperationType.ADD, "depth" : 5 * mm});
        }
        {
            var Q0;
            Q0=makeQuery(id+"F10.opExtrude","CAP_FACE",FACE,{"disambiguationData":[OSD([sQuery(id+"F9.wireOp",EDGE,"E120.bottom"),sQuery(id+"F9.wireOp",EDGE,"E120.top"),sQuery(id+"F9.wireOp",EDGE,"E120.left"),sQuery(id+"F9.wireOp",EDGE,"E120.right"),sQuery(id+"F9.wireOp",EDGE,"E121.0"),sQuery(id+"F9.wireOp",EDGE,"E121.1"),sQuery(id+"F9.wireOp",EDGE,"E121.2"),sQuery(id+"F9.wireOp",EDGE,"E121.3")])],"isStart":false});
            var sketch = newSketch(context, id + "F11", { "sketchPlane" : qUnion([Q0])});
            skPoint(sketch, "E122.0", {"position": v(-121.72, 49.3) * mm});
            skLineSegment(sketch, "E123.bottom", {"start": v(-112.62, 48.8) * mm, "end": v(-130.82, 48.8) * mm});
            skLineSegment(sketch, "E123.top", {"start": v(-112.62, 49.8) * mm, "end": v(-130.82, 49.8) * mm});
            skLineSegment(sketch, "E123.left", {"start": v(-112.62, 48.8) * mm, "end": v(-112.62, 49.8) * mm});
            skLineSegment(sketch, "E123.right", {"start": v(-130.82, 48.8) * mm, "end": v(-130.82, 49.8) * mm});
            skLineSegment(sketch, "E124.bottom", {"start": v(-121.22, 40.2) * mm, "end": v(-122.22, 40.2) * mm});
            skLineSegment(sketch, "E124.top", {"start": v(-121.22, 58.4) * mm, "end": v(-122.22, 58.4) * mm});
            skLineSegment(sketch, "E124.left", {"start": v(-121.22, 40.2) * mm, "end": v(-121.22, 58.4) * mm});
            skLineSegment(sketch, "E124.right", {"start": v(-122.22, 40.2) * mm, "end": v(-122.22, 58.4) * mm});
            skSolve(sketch);
        }
        {
            var Q0;
            Q0=makeQuery(id+"FvrxBWBR3NFs59h_1.boolean.opBoolean","MERGE",FACE,{"derivedFrom":[makeQuery(id+"F5.boolean.opBoolean","COPY",FACE,{"derivedFrom":makeQuery(id+"F5.opExtrude","CAP_FACE",FACE,{"disambiguationData":[OSD([sQuery(id+"F4.wireOp",EDGE,"E94.bottom"),sQuery(id+"F4.wireOp",EDGE,"E94.top"),sQuery(id+"F4.wireOp",EDGE,"E94.left"),sQuery(id+"F4.wireOp",EDGE,"E94.right")])],"isStart":false})}),makeQuery(id+"FvrxBWBR3NFs59h_1.opExtrude","CAP_FACE",FACE,{"disambiguationData":[OSD([sQuery(id+"FOyiDT4y5zkIJA3_1.wireOp",EDGE,"oN5qgFBu-MPa5-jxRP-8K83-Y7W6XuHjnRPn.bottom"),sQuery(id+"FOyiDT4y5zkIJA3_1.wireOp",EDGE,"oN5qgFBu-MPa5-jxRP-8K83-Y7W6XuHjnRPn.top"),sQuery(id+"FOyiDT4y5zkIJA3_1.wireOp",EDGE,"oN5qgFBu-MPa5-jxRP-8K83-Y7W6XuHjnRPn.left"),sQuery(id+"FOyiDT4y5zkIJA3_1.wireOp",EDGE,"oN5qgFBu-MPa5-jxRP-8K83-Y7W6XuHjnRPn.right")])],"isStart":false}),makeQuery(id+"FvrxBWBR3NFs59h_1.opExtrude","CAP_FACE",FACE,{"disambiguationData":[OSD([sQuery(id+"FOyiDT4y5zkIJA3_1.wireOp",EDGE,"if443p5T-YKs4-1gVt-ORIe-qeo7ftMrQxsQ.bottom"),sQuery(id+"FOyiDT4y5zkIJA3_1.wireOp",EDGE,"if443p5T-YKs4-1gVt-ORIe-qeo7ftMrQxsQ.top"),sQuery(id+"FOyiDT4y5zkIJA3_1.wireOp",EDGE,"if443p5T-YKs4-1gVt-ORIe-qeo7ftMrQxsQ.left"),sQuery(id+"FOyiDT4y5zkIJA3_1.wireOp",EDGE,"if443p5T-YKs4-1gVt-ORIe-qeo7ftMrQxsQ.right")])],"isStart":false})]});
            var sketch = newSketch(context, id + "F12", { "sketchPlane" : qUnion([Q0])});
            skPoint(sketch, "E125.0", {"position": v(-109.5, 1.96) * mm});
            skLineSegment(sketch, "E126.bottom", {"start": v(-106.5, -1.04) * mm, "end": v(-112.5, -1.04) * mm});
            skLineSegment(sketch, "E126.top", {"start": v(-106.5, 4.96) * mm, "end": v(-112.5, 4.96) * mm});
            skLineSegment(sketch, "E126.left", {"start": v(-106.5, -1.04) * mm, "end": v(-106.5, 4.96) * mm});
            skLineSegment(sketch, "E126.right", {"start": v(-112.5, -1.04) * mm, "end": v(-112.5, 4.96) * mm});
            skSolve(sketch);
        }
        {
            var Q0;
            {var subQ0=sQuery(id+"F12.wireOp",EDGE,"E126.top");Q0=makeQuery(id+"F12.imprint","IMPRINT",FACE,{"disambiguationData":[TD([[makeQuery(id+"F12.imprint","IMPRINT",EDGE,{"derivedFrom":subQ0}),1.0]])]});}
            var Q1;
            {var subQ0=sQuery(id+"F12.wireOp",EDGE,"E126.left");var subQ1=makeQuery(id+"F5.opExtrude","CAP_FACE",FACE,{"disambiguationData":[OSD([sQuery(id+"F4.wireOp",EDGE,"E94.bottom"),sQuery(id+"F4.wireOp",EDGE,"E94.top"),sQuery(id+"F4.wireOp",EDGE,"E94.left"),sQuery(id+"F4.wireOp",EDGE,"E94.right")])],"isStart":false});var subQ2=sQuery(id+"F0.wireOp",EDGE,"E31.trimOffspring");var subQ3=makeQuery(id+"F5.boolean.opBoolean","INTERSECT",EDGE,{"derivedFrom":[makeQuery(id+"F3.boolean.opBoolean","MERGE",FACE,{"derivedFrom":[makeQuery(id+"F2.opExtrude","SWEPT_FACE",FACE,{"disambiguationData":[OSD([subQ2])]}),makeQuery(id+"F3.opExtrude","SWEPT_FACE",FACE,{"disambiguationData":[OSD([subQ2])]})]}),subQ1]});var subQ4=makeQuery(id+"F12.imprint","INTERSECT",VERTEX,{"derivedFrom":[subQ3,subQ0]});Q1=makeQuery(id+"F12.imprint","IMPRINT",FACE,{"disambiguationData":[TD([[makeQuery(id+"F12.imprint","IMPRINT",EDGE,{"disambiguationData":[TD([[subQ4,-1.0]])],"derivedFrom":subQ0}),1.0]])]});}
            var Q2;
            {var subQ0=sQuery(id+"F12.wireOp",EDGE,"E126.bottom");Q2=makeQuery(id+"F12.imprint","IMPRINT",FACE,{"disambiguationData":[TD([[makeQuery(id+"F12.imprint","IMPRINT",EDGE,{"derivedFrom":subQ0}),-1.0]])]});}
            extrude(context, id + "F13", {"entities" : qUnion([Q0, Q1, Q2]), "operationType" : NewBodyOperationType.ADD, "depth" : 8 * mm});
        }
        {
            var Q0;
            Q0=qSketchRegion(id+"F11",true);
            extrude(context, id + "F14", {"entities" : qUnion([Q0]), "operationType" : NewBodyOperationType.ADD, "oppositeDirection" : true, "depth" : 6 * mm});
        }
        {
            var Q0;
            Q0=makeQuery(id+"F14.boolean.opBoolean","MERGE",FACE,{"derivedFrom":[makeQuery(id+"F10.opExtrude","CAP_FACE",FACE,{"disambiguationData":[OSD([sQuery(id+"F9.wireOp",EDGE,"E120.bottom"),sQuery(id+"F9.wireOp",EDGE,"E120.top"),sQuery(id+"F9.wireOp",EDGE,"E120.left"),sQuery(id+"F9.wireOp",EDGE,"E120.right"),sQuery(id+"F9.wireOp",EDGE,"E121.0"),sQuery(id+"F9.wireOp",EDGE,"E121.1"),sQuery(id+"F9.wireOp",EDGE,"E121.2"),sQuery(id+"F9.wireOp",EDGE,"E121.3")])],"isStart":false}),makeQuery(id+"F14.opExtrude","CAP_FACE",FACE,{"disambiguationData":[OSD([sQuery(id+"F11.wireOp",EDGE,"E123.bottom"),sQuery(id+"F11.wireOp",EDGE,"E123.top"),sQuery(id+"F11.wireOp",EDGE,"E123.left"),sQuery(id+"F11.wireOp",EDGE,"E123.right"),sQuery(id+"F11.wireOp",EDGE,"E124.bottom"),sQuery(id+"F11.wireOp",EDGE,"E124.top"),sQuery(id+"F11.wireOp",EDGE,"E124.left"),sQuery(id+"F11.wireOp",EDGE,"E124.right")])],"isStart":true})]});
            var sketch = newSketch(context, id + "F15", { "sketchPlane" : qUnion([Q0])});
            skPoint(sketch, "E127.0", {"position": v(-130.82, 58.4) * mm});
            skPoint(sketch, "E127.1", {"position": v(-112.62, 40.2) * mm});
            skLineSegment(sketch, "E128.bottom", {"start": v(-130.82, 58.4) * mm, "end": v(-112.62, 58.4) * mm});
            skLineSegment(sketch, "E128.top", {"start": v(-130.82, 40.2) * mm, "end": v(-112.62, 40.2) * mm});
            skLineSegment(sketch, "E128.left", {"start": v(-130.82, 58.4) * mm, "end": v(-130.82, 40.2) * mm});
            skLineSegment(sketch, "E128.right", {"start": v(-112.62, 58.4) * mm, "end": v(-112.62, 40.2) * mm});
            skSolve(sketch);
        }
        {
            var Q0;
            Q0=qSketchRegion(id+"F15",true);
            extrude(context, id + "F16", {"entities" : qUnion([Q0]), "operationType" : NewBodyOperationType.REMOVE, "oppositeDirection" : true, "depth" : 1 * mm});
        }
        {
            var Q0;
            {var subQ0=sQuery(id+"F6.wireOp",EDGE,"E117.right");var subQ2=sQuery(id+"F6.wireOp",EDGE,"E118.right");var subQ4=sQuery(id+"F6.wireOp",EDGE,"E116.left");var subQ6=sQuery(id+"F6.wireOp",EDGE,"E118.left");var subQ8=sQuery(id+"F6.wireOp",EDGE,"E115.top");var subQ9=sQuery(id+"F6.wireOp",EDGE,"E115.left");var subQ11=sQuery(id+"F6.wireOp",EDGE,"E115.right");var subQ13=sQuery(id+"F6.wireOp",EDGE,"E118.top");var subQ16=sQuery(id+"F6.wireOp",EDGE,"E118.bottom");var subQ17=sQuery(id+"F6.wireOp",EDGE,"E115.bottom");var subQ18=makeQuery(id+"F7.opExtrude","CAP_FACE",FACE,{"disambiguationData":[OSD([subQ17,subQ8,subQ9,subQ11,subQ4,subQ0,subQ16,subQ13,subQ6,subQ2])],"isStart":true});Q0=makeQuery(id+"F14.boolean.opBoolean","MERGE",FACE,{"derivedFrom":[makeQuery(id+"F8.boolean.opBoolean","SPLIT",FACE,{"disambiguationData":[TD([makeQuery(id+"F7.opExtrude","SWEPT_FACE",FACE,{"disambiguationData":[OSD([subQ17])]})])],"derivedFrom":subQ18}),makeQuery(id+"F8.boolean.opBoolean","SPLIT",FACE,{"disambiguationData":[TD([makeQuery(id+"F7.opExtrude","SWEPT_FACE",FACE,{"disambiguationData":[OSD([subQ8])]})])],"derivedFrom":subQ18}),makeQuery(id+"F14.opExtrude","CAP_FACE",FACE,{"disambiguationData":[OSD([sQuery(id+"F11.wireOp",EDGE,"E123.bottom"),sQuery(id+"F11.wireOp",EDGE,"E123.top"),sQuery(id+"F11.wireOp",EDGE,"E123.left"),sQuery(id+"F11.wireOp",EDGE,"E123.right"),sQuery(id+"F11.wireOp",EDGE,"E124.bottom"),sQuery(id+"F11.wireOp",EDGE,"E124.top"),sQuery(id+"F11.wireOp",EDGE,"E124.left"),sQuery(id+"F11.wireOp",EDGE,"E124.right")])],"isStart":false})]});}
            var sketch = newSketch(context, id + "F17", { "sketchPlane" : qUnion([Q0])});
            skPoint(sketch, "E129.0", {"position": v(-121.72, -40.2) * mm});
            skLineSegment(sketch, "E130.bottom", {"start": v(-120.72, -50.54) * mm, "end": v(-122.72, -50.54) * mm});
            skLineSegment(sketch, "E130.top", {"start": v(-120.72, -48.04) * mm, "end": v(-122.72, -48.04) * mm});
            skLineSegment(sketch, "E130.left", {"start": v(-120.72, -50.54) * mm, "end": v(-120.72, -48.04) * mm});
            skLineSegment(sketch, "E130.right", {"start": v(-122.72, -50.54) * mm, "end": v(-122.72, -48.04) * mm});
            skPoint(sketch, "E130.middle", {"position": v(-121.72, -49.3) * mm});
            skPoint(sketch, "E130.middle.positionSnap0", {"position": v(-130.82, -49.3) * mm});
            skPoint(sketch, "E130.centerSnap0", {"position": v(-130.82, -49.3) * mm});
            skSolve(sketch);
        }
        {
            var Q0;
            Q0=makeQuery(id+"F13.opExtrude","CAP_FACE",FACE,{"disambiguationData":[OSD([sQuery(id+"F12.wireOp",EDGE,"E126.bottom"),sQuery(id+"F12.wireOp",EDGE,"E126.top"),sQuery(id+"F12.wireOp",EDGE,"E126.left"),sQuery(id+"F12.wireOp",EDGE,"E126.right")])],"isStart":false});
            var sketch = newSketch(context, id + "F18", { "sketchPlane" : qUnion([Q0])});
            skPoint(sketch, "E131.0", {"position": v(-109.5, 1.96) * mm});
            skLineSegment(sketch, "E132.bottom", {"start": v(-108.5, 0.7) * mm, "end": v(-110.5, 0.7) * mm});
            skLineSegment(sketch, "E132.top", {"start": v(-108.5, 3.2) * mm, "end": v(-110.5, 3.2) * mm});
            skLineSegment(sketch, "E132.left", {"start": v(-108.5, 0.7) * mm, "end": v(-108.5, 3.2) * mm});
            skLineSegment(sketch, "E132.right", {"start": v(-110.5, 0.7) * mm, "end": v(-110.5, 3.2) * mm});
            skSolve(sketch);
        }
        {
            var Q0;
            Q0=qSketchRegion(id+"F18",true);
            extrude(context, id + "F19", {"entities" : qUnion([Q0]), "operationType" : NewBodyOperationType.ADD, "depth" : 2 * mm});
        }
        {
            var Q0;
            {var subQ0=sQuery(id+"F11.wireOp",EDGE,"E123.right");var subQ1=sQuery(id+"F11.wireOp",EDGE,"E123.bottom");var subQ4=sQuery(id+"F11.wireOp",EDGE,"E124.right");var subQ5=sQuery(id+"F6.wireOp",EDGE,"E118.right");var subQ8=sQuery(id+"F11.wireOp",EDGE,"E123.top");var subQ9=sQuery(id+"F6.wireOp",EDGE,"E117.right");var subQ11=sQuery(id+"F6.wireOp",EDGE,"E116.left");var subQ13=sQuery(id+"F6.wireOp",EDGE,"E118.left");var subQ15=sQuery(id+"F6.wireOp",EDGE,"E115.top");var subQ16=sQuery(id+"F6.wireOp",EDGE,"E115.left");var subQ18=sQuery(id+"F6.wireOp",EDGE,"E115.right");var subQ20=sQuery(id+"F6.wireOp",EDGE,"E118.top");var subQ22=sQuery(id+"F6.wireOp",EDGE,"E118.bottom");var subQ23=sQuery(id+"F6.wireOp",EDGE,"E115.bottom");var subQ24=makeQuery(id+"F7.opExtrude","CAP_FACE",FACE,{"disambiguationData":[OSD([subQ23,subQ15,subQ16,subQ18,subQ11,subQ9,subQ22,subQ20,subQ13,subQ5])],"isStart":true});Q0=makeQuery(id+"F22.boolean.opBoolean","SPLIT",FACE,{"disambiguationData":[TD([makeQuery(id+"F22.opExtrude","SWEPT_FACE",FACE,{"disambiguationData":[OSD([sQuery(id+"F17.wireOp",EDGE,"E130.right")])]})])],"derivedFrom":makeQuery(id+"F14.boolean.opBoolean","MERGE",FACE,{"derivedFrom":[makeQuery(id+"F8.boolean.opBoolean","SPLIT",FACE,{"disambiguationData":[TD([makeQuery(id+"F7.opExtrude","SWEPT_FACE",FACE,{"disambiguationData":[OSD([subQ23])]})])],"derivedFrom":subQ24}),makeQuery(id+"F8.boolean.opBoolean","SPLIT",FACE,{"disambiguationData":[TD([makeQuery(id+"F7.opExtrude","SWEPT_FACE",FACE,{"disambiguationData":[OSD([subQ15])]})])],"derivedFrom":subQ24}),makeQuery(id+"F14.opExtrude","CAP_FACE",FACE,{"disambiguationData":[OSD([subQ1,subQ8,sQuery(id+"F11.wireOp",EDGE,"E123.left"),subQ0,sQuery(id+"F11.wireOp",EDGE,"E124.bottom"),sQuery(id+"F11.wireOp",EDGE,"E124.top"),sQuery(id+"F11.wireOp",EDGE,"E124.left"),subQ4])],"isStart":false})]})});}
            var sketch = newSketch(context, id + "F20", { "sketchPlane" : qUnion([Q0])});
            skPoint(sketch, "E133.0", {"position": v(-126.52, -48.8) * mm});
            skPoint(sketch, "E134.0", {"position": v(-122.22, -44.5) * mm});
            skPoint(sketch, "E135.0", {"position": v(-122.22, -40.2) * mm});
            skLineSegment(sketch, "E136.bottom", {"start": v(-122.22, -40.2) * mm, "end": v(-130.82, -40.2) * mm});
            skLineSegment(sketch, "E136.top", {"start": v(-122.22, -48.8) * mm, "end": v(-130.82, -48.8) * mm});
            skLineSegment(sketch, "E136.left", {"start": v(-122.22, -40.2) * mm, "end": v(-122.22, -48.8) * mm});
            skLineSegment(sketch, "E136.right", {"start": v(-130.82, -40.2) * mm, "end": v(-130.82, -48.8) * mm});
            skPoint(sketch, "E136.middle", {"position": v(-126.52, -44.5) * mm});
            skLineSegment(sketch, "E137.bottom", {"start": v(-122.72, -40.7) * mm, "end": v(-130.32, -40.7) * mm});
            skLineSegment(sketch, "E137.top", {"start": v(-122.72, -48.3) * mm, "end": v(-130.32, -48.3) * mm});
            skLineSegment(sketch, "E137.left", {"start": v(-122.72, -40.7) * mm, "end": v(-122.72, -48.3) * mm});
            skLineSegment(sketch, "E137.right", {"start": v(-130.32, -40.7) * mm, "end": v(-130.32, -48.3) * mm});
            skLineSegment(sketch, "E138.direction1", {"start": v(-130.82, -48.8) * mm, "end": v(-121.22, -48.8) * mm, "construction": true});
            skLineSegment(sketch, "E139.0.1.0", {"start": v(-113.12, -40.7) * mm, "end": v(-120.72, -40.7) * mm});
            skLineSegment(sketch, "E139.3.1.0", {"start": v(-112.62, -40.2) * mm, "end": v(-121.22, -40.2) * mm});
            skLineSegment(sketch, "E139.6.1.0", {"start": v(-112.62, -48.8) * mm, "end": v(-121.22, -48.8) * mm});
            skLineSegment(sketch, "E139.9.1.0", {"start": v(-112.62, -40.2) * mm, "end": v(-112.62, -48.8) * mm});
            skPoint(sketch, "E139.12.1.0", {"position": v(-116.92, -44.5) * mm});
            skLineSegment(sketch, "E139.13.1.0", {"start": v(-113.12, -40.7) * mm, "end": v(-113.12, -48.3) * mm});
            skLineSegment(sketch, "E139.16.1.0", {"start": v(-120.72, -40.7) * mm, "end": v(-120.72, -48.3) * mm});
            skLineSegment(sketch, "E139.19.1.0", {"start": v(-121.22, -40.2) * mm, "end": v(-121.22, -48.8) * mm});
            skPoint(sketch, "E139.22.1.0", {"position": v(-112.62, -44.5) * mm});
            skPoint(sketch, "E139.23.1.0", {"position": v(-112.62, -40.2) * mm});
            skLineSegment(sketch, "E139.24.1.0", {"start": v(-113.12, -48.3) * mm, "end": v(-120.72, -48.3) * mm});
            skPoint(sketch, "E139.27.1.0", {"position": v(-116.92, -48.8) * mm});
            skPoint(sketch, "E139.28.1.0", {"position": v(-116.92, -44.5) * mm});
            skSolve(sketch);
        }
        {
            var Q0;
            Q0=qSketchRegion(id+"F20",true);
            extrude(context, id + "F21", {"entities" : qUnion([Q0]), "operationType" : NewBodyOperationType.ADD, "oppositeDirection" : true, "depth" : 2 * mm});
        }
        {
            var Q0;
            Q0=qSketchRegion(id+"F17",true);
            extrude(context, id + "F22", {"entities" : qUnion([Q0]), "operationType" : NewBodyOperationType.REMOVE, "oppositeDirection" : true, "depth" : 2 * mm});
        }
        {
            var Q0;
            Q0=makeQuery(id+"F0.imprint","IMPRINT",FACE,{"disambiguationData":[TD([[makeQuery(id+"F0.imprint","IMPRINT",EDGE,{"derivedFrom":sQuery(id+"F0.wireOp",EDGE,"E0.bottom")}),-1.0]])]});
            var sketch = newSketch(context, id + "F23", { "sketchPlane" : qUnion([Q0])});
            skLineSegment(sketch, "E140.top", {"start": v(-139.5, -33.04) * mm, "end": v(-43.5, -33.04) * mm});
            skLineSegment(sketch, "E140.left", {"start": v(-139.5, -55.04) * mm, "end": v(-139.5, -33.04) * mm});
            skLineSegment(sketch, "E141.top", {"start": v(-25.5, -11.04) * mm, "end": v(-43.5, -11.04) * mm});
            skLineSegment(sketch, "E141.right", {"start": v(-43.5, -33.04) * mm, "end": v(-43.5, -11.04) * mm});
            skLineSegment(sketch, "E142.top", {"start": v(-9.5, 11.96) * mm, "end": v(-25.5, 11.96) * mm});
            skLineSegment(sketch, "E142.right", {"start": v(-25.5, -11.04) * mm, "end": v(-25.5, 11.96) * mm});
            skLineSegment(sketch, "E143", {"start": v(-9.5, 11.96) * mm, "end": v(-9.5, -55.04) * mm});
            skLineSegment(sketch, "E144", {"start": v(-139.5, -55.04) * mm, "end": v(-9.5, -55.04) * mm});
            skLineSegment(sketch, "E145.bottom", {"start": v(-43.5, -33.04) * mm, "end": v(-9.5, -33.04) * mm});
            skLineSegment(sketch, "E145.top", {"start": v(-43.5, -31.04) * mm, "end": v(-9.5, -31.04) * mm});
            skLineSegment(sketch, "E145.left", {"start": v(-43.5, -33.04) * mm, "end": v(-43.5, -31.04) * mm});
            skLineSegment(sketch, "E145.right", {"start": v(-9.5, -33.04) * mm, "end": v(-9.5, -31.04) * mm});
            skLineSegment(sketch, "E146.bottom", {"start": v(-25.5, -11.04) * mm, "end": v(-9.5, -11.04) * mm});
            skLineSegment(sketch, "E146.top", {"start": v(-25.5, -9.04) * mm, "end": v(-9.5, -9.04) * mm});
            skLineSegment(sketch, "E146.left", {"start": v(-25.5, -11.04) * mm, "end": v(-25.5, -9.04) * mm});
            skLineSegment(sketch, "E146.right", {"start": v(-9.5, -11.04) * mm, "end": v(-9.5, -9.04) * mm});
            skSolve(sketch);
        }
        {
            var Q0;
            Q0=makeQuery(id+"F23.imprint","IMPRINT",FACE,{"disambiguationData":[TD([[makeQuery(id+"F23.imprint","IMPRINT",EDGE,{"derivedFrom":makeQuery(id+"F0.imprint","IMPRINT",EDGE,{"derivedFrom":sQuery(id+"F0.wireOp",EDGE,"E3")})}),1.0]])]});
            var Q1;
            Q1=makeQuery(id+"F23.imprint","IMPRINT",FACE,{"disambiguationData":[TD([[makeQuery(id+"F23.imprint","IMPRINT",EDGE,{"derivedFrom":makeQuery(id+"F0.imprint","IMPRINT",EDGE,{"derivedFrom":sQuery(id+"F0.wireOp",EDGE,"E4")})}),1.0]])]});
            var Q2;
            Q2=makeQuery(id+"F23.imprint","IMPRINT",FACE,{"disambiguationData":[TD([[makeQuery(id+"F23.imprint","IMPRINT",EDGE,{"derivedFrom":makeQuery(id+"F0.imprint","IMPRINT",EDGE,{"derivedFrom":sQuery(id+"F0.wireOp",EDGE,"E5")})}),1.0]])]});
            var Q3;
            Q3=makeQuery(id+"F23.imprint","IMPRINT",FACE,{"disambiguationData":[TD([[makeQuery(id+"F23.imprint","IMPRINT",EDGE,{"derivedFrom":makeQuery(id+"F0.imprint","IMPRINT",EDGE,{"derivedFrom":sQuery(id+"F0.wireOp",EDGE,"E8")})}),1.0]])]});
            var Q4;
            Q4=makeQuery(id+"F23.imprint","IMPRINT",FACE,{"disambiguationData":[TD([[makeQuery(id+"F23.imprint","IMPRINT",EDGE,{"derivedFrom":makeQuery(id+"F0.imprint","IMPRINT",EDGE,{"derivedFrom":sQuery(id+"F0.wireOp",EDGE,"E9")})}),1.0]])]});
            var Q5;
            Q5=makeQuery(id+"F23.imprint","IMPRINT",FACE,{"disambiguationData":[TD([[makeQuery(id+"F23.imprint","IMPRINT",EDGE,{"derivedFrom":makeQuery(id+"F0.imprint","IMPRINT",EDGE,{"derivedFrom":sQuery(id+"F0.wireOp",EDGE,"E10")})}),1.0]])]});
            var Q6;
            Q6=makeQuery(id+"F23.imprint","IMPRINT",FACE,{"disambiguationData":[TD([[makeQuery(id+"F23.imprint","IMPRINT",EDGE,{"derivedFrom":makeQuery(id+"F0.imprint","IMPRINT",EDGE,{"derivedFrom":sQuery(id+"F0.wireOp",EDGE,"E11")})}),1.0]])]});
            var Q7;
            Q7=makeQuery(id+"F23.imprint","IMPRINT",FACE,{"disambiguationData":[TD([[makeQuery(id+"F23.imprint","IMPRINT",EDGE,{"derivedFrom":makeQuery(id+"F0.imprint","IMPRINT",EDGE,{"derivedFrom":sQuery(id+"F0.wireOp",EDGE,"E12")})}),1.0]])]});
            var Q8;
            Q8=makeQuery(id+"F23.imprint","IMPRINT",FACE,{"disambiguationData":[TD([[makeQuery(id+"F23.imprint","IMPRINT",EDGE,{"derivedFrom":makeQuery(id+"F0.imprint","IMPRINT",EDGE,{"derivedFrom":sQuery(id+"F0.wireOp",EDGE,"E13")})}),1.0]])]});
            var Q9;
            Q9=makeQuery(id+"F23.imprint","IMPRINT",FACE,{"disambiguationData":[TD([[makeQuery(id+"F23.imprint","IMPRINT",EDGE,{"derivedFrom":makeQuery(id+"F0.imprint","IMPRINT",EDGE,{"derivedFrom":sQuery(id+"F0.wireOp",EDGE,"E14")})}),1.0]])]});
            var Q10;
            Q10=makeQuery(id+"F23.imprint","IMPRINT",FACE,{"disambiguationData":[TD([[makeQuery(id+"F23.imprint","IMPRINT",EDGE,{"derivedFrom":makeQuery(id+"F0.imprint","IMPRINT",EDGE,{"derivedFrom":sQuery(id+"F0.wireOp",EDGE,"E16")})}),1.0]])]});
            var Q11;
            Q11=makeQuery(id+"F23.imprint","IMPRINT",FACE,{"disambiguationData":[TD([[makeQuery(id+"F23.imprint","IMPRINT",EDGE,{"derivedFrom":makeQuery(id+"F0.imprint","IMPRINT",EDGE,{"derivedFrom":sQuery(id+"F0.wireOp",EDGE,"E17")})}),1.0]])]});
            var Q12;
            {var subQ1=sQuery(id+"F23.wireOp",EDGE,"E142.top");Q12=makeQuery(id+"F23.imprint","IMPRINT",FACE,{"disambiguationData":[TD([[makeQuery(id+"F23.imprint","IMPRINT",EDGE,{"derivedFrom":subQ1}),1.0]])]});}
            var Q13;
            Q13=makeQuery(id+"F23.imprint","IMPRINT",FACE,{"disambiguationData":[TD([[makeQuery(id+"F23.imprint","IMPRINT",EDGE,{"derivedFrom":sQuery(id+"F23.wireOp",EDGE,"E141.top")}),1.0]])]});
            var Q14;
            Q14=makeQuery(id+"F23.imprint","IMPRINT",FACE,{"disambiguationData":[TD([[makeQuery(id+"F23.imprint","IMPRINT",EDGE,{"derivedFrom":sQuery(id+"F23.wireOp",EDGE,"E140.top")}),-1.0]])]});
            extrude(context, id + "F24", {"entities" : qUnion([Q0, Q1, Q2, Q3, Q4, Q5, Q6, Q7, Q8, Q9, Q10, Q11, Q12, Q13, Q14]), "operationType" : NewBodyOperationType.REMOVE, "depth" : 5 * mm});
        }
        {
            var Q0;
            Q0=makeQuery(id+"F1.imprint","IMPRINT",FACE,{"disambiguationData":[TD([[makeQuery(id+"F1.imprint","IMPRINT",EDGE,{"derivedFrom":sQuery(id+"F1.wireOp",EDGE,"E53.bottom")}),-1.0]])]});
            var Q1;
            {var subQ0=sQuery(id+"F1.wireOp",EDGE,"E75.right");var subQ1=sQuery(id+"F1.wireOp",EDGE,"E75.top");var subQ2=makeQuery(id+"F1.imprint","INTERSECT",VERTEX,{"derivedFrom":[subQ1,subQ0]});Q1=makeQuery(id+"F1.imprint","IMPRINT",FACE,{"disambiguationData":[TD([[makeQuery(id+"F1.imprint","IMPRINT",EDGE,{"disambiguationData":[TD([[subQ2,1.0]])],"derivedFrom":subQ1}),1.0]])]});}
            var Q2;
            {var subQ0=sQuery(id+"F1.wireOp",EDGE,"E75.left");var subQ1=sQuery(id+"F1.wireOp",EDGE,"E75.top");var subQ2=makeQuery(id+"F1.imprint","INTERSECT",VERTEX,{"derivedFrom":[subQ1,subQ0]});Q2=makeQuery(id+"F1.imprint","IMPRINT",FACE,{"disambiguationData":[TD([[makeQuery(id+"F1.imprint","IMPRINT",EDGE,{"disambiguationData":[TD([[subQ2,-1.0]])],"derivedFrom":subQ1}),1.0]])]});}
            var Q3;
            {var subQ0=sQuery(id+"F1.wireOp",EDGE,"E75.right");var subQ1=sQuery(id+"F1.wireOp",EDGE,"E75.bottom");var subQ2=makeQuery(id+"F1.imprint","INTERSECT",VERTEX,{"derivedFrom":[subQ1,subQ0]});Q3=makeQuery(id+"F1.imprint","IMPRINT",FACE,{"disambiguationData":[TD([[makeQuery(id+"F1.imprint","IMPRINT",EDGE,{"disambiguationData":[TD([[subQ2,1.0]])],"derivedFrom":subQ1}),-1.0]])]});}
            var Q4;
            {var subQ0=sQuery(id+"F1.wireOp",EDGE,"E75.left");var subQ1=sQuery(id+"F1.wireOp",EDGE,"E75.bottom");var subQ2=makeQuery(id+"F1.imprint","INTERSECT",VERTEX,{"derivedFrom":[subQ1,subQ0]});Q4=makeQuery(id+"F1.imprint","IMPRINT",FACE,{"disambiguationData":[TD([[makeQuery(id+"F1.imprint","IMPRINT",EDGE,{"disambiguationData":[TD([[subQ2,-1.0]])],"derivedFrom":subQ1}),-1.0]])]});}
            var Q5;
            {var subQ0=sQuery(id+"F1.wireOp",EDGE,"E74.right");var subQ1=sQuery(id+"F1.wireOp",EDGE,"E74.top");var subQ2=makeQuery(id+"F1.imprint","INTERSECT",VERTEX,{"derivedFrom":[subQ1,subQ0]});Q5=makeQuery(id+"F1.imprint","IMPRINT",FACE,{"disambiguationData":[TD([[makeQuery(id+"F1.imprint","IMPRINT",EDGE,{"disambiguationData":[TD([[subQ2,1.0]])],"derivedFrom":subQ1}),1.0]])]});}
            var Q6;
            {var subQ0=sQuery(id+"F1.wireOp",EDGE,"E74.left");var subQ1=sQuery(id+"F1.wireOp",EDGE,"E74.top");var subQ2=makeQuery(id+"F1.imprint","INTERSECT",VERTEX,{"derivedFrom":[subQ1,subQ0]});Q6=makeQuery(id+"F1.imprint","IMPRINT",FACE,{"disambiguationData":[TD([[makeQuery(id+"F1.imprint","IMPRINT",EDGE,{"disambiguationData":[TD([[subQ2,-1.0]])],"derivedFrom":subQ1}),1.0]])]});}
            var Q7;
            {var subQ0=sQuery(id+"F1.wireOp",EDGE,"E74.right");var subQ1=sQuery(id+"F1.wireOp",EDGE,"E74.bottom");var subQ2=makeQuery(id+"F1.imprint","INTERSECT",VERTEX,{"derivedFrom":[subQ1,subQ0]});Q7=makeQuery(id+"F1.imprint","IMPRINT",FACE,{"disambiguationData":[TD([[makeQuery(id+"F1.imprint","IMPRINT",EDGE,{"disambiguationData":[TD([[subQ2,1.0]])],"derivedFrom":subQ1}),-1.0]])]});}
            var Q8;
            {var subQ0=sQuery(id+"F1.wireOp",EDGE,"E74.left");var subQ1=sQuery(id+"F1.wireOp",EDGE,"E74.bottom");var subQ2=makeQuery(id+"F1.imprint","INTERSECT",VERTEX,{"derivedFrom":[subQ1,subQ0]});Q8=makeQuery(id+"F1.imprint","IMPRINT",FACE,{"disambiguationData":[TD([[makeQuery(id+"F1.imprint","IMPRINT",EDGE,{"disambiguationData":[TD([[subQ2,-1.0]])],"derivedFrom":subQ1}),-1.0]])]});}
            extrude(context, id + "F25", {"entities" : qUnion([Q0, Q1, Q2, Q3, Q4, Q5, Q6, Q7, Q8]), "depth" : 2 * mm});
        }
        {
            var Q0;
            Q0=makeQuery(id+"F3.opExtrude","CAP_FACE",FACE,{"disambiguationData":[OSD([sQuery(id+"F0.wireOp",EDGE,"E0.bottom"),sQuery(id+"F0.wireOp",EDGE,"E0.top"),sQuery(id+"F0.wireOp",EDGE,"E0.left"),sQuery(id+"F0.wireOp",EDGE,"E0.right"),sQuery(id+"F0.wireOp",EDGE,"E3"),sQuery(id+"F0.wireOp",EDGE,"E4"),sQuery(id+"F0.wireOp",EDGE,"E5"),sQuery(id+"F0.wireOp",EDGE,"E8"),sQuery(id+"F0.wireOp",EDGE,"E9"),sQuery(id+"F0.wireOp",EDGE,"E10"),sQuery(id+"F0.wireOp",EDGE,"E11"),sQuery(id+"F0.wireOp",EDGE,"E12"),sQuery(id+"F0.wireOp",EDGE,"E13"),sQuery(id+"F0.wireOp",EDGE,"E14"),sQuery(id+"F0.wireOp",EDGE,"E15.bottom"),sQuery(id+"F0.wireOp",EDGE,"E15.top"),sQuery(id+"F0.wireOp",EDGE,"E15.left"),sQuery(id+"F0.wireOp",EDGE,"E15.right"),sQuery(id+"F0.wireOp",EDGE,"E16"),sQuery(id+"F0.wireOp",EDGE,"E17"),sQuery(id+"F0.wireOp",EDGE,"E19.bottom"),sQuery(id+"F0.wireOp",EDGE,"E19.top"),sQuery(id+"F0.wireOp",EDGE,"E19.left"),sQuery(id+"F0.wireOp",EDGE,"E19.right"),sQuery(id+"F0.wireOp",EDGE,"E21.bottom"),sQuery(id+"F0.wireOp",EDGE,"E21.top"),sQuery(id+"F0.wireOp",EDGE,"E22.left"),sQuery(id+"F0.wireOp",EDGE,"E22.right"),sQuery(id+"F0.wireOp",EDGE,"E23.left"),sQuery(id+"F0.wireOp",EDGE,"E23.right"),sQuery(id+"F0.wireOp",EDGE,"E24.trimOffspring"),sQuery(id+"F0.wireOp",EDGE,"E25.trimOffspring"),sQuery(id+"F0.wireOp",EDGE,"E26.trimOffspring"),sQuery(id+"F0.wireOp",EDGE,"E27.trimOffspring"),sQuery(id+"F0.wireOp",EDGE,"E28.trimOffspring"),sQuery(id+"F0.wireOp",EDGE,"E29.trimOffspring"),sQuery(id+"F0.wireOp",EDGE,"E30.trimOffspring"),sQuery(id+"F0.wireOp",EDGE,"E31.trimOffspring"),sQuery(id+"F0.wireOp",EDGE,"E20.bottom"),sQuery(id+"F0.wireOp",EDGE,"E20.top"),sQuery(id+"F0.wireOp",EDGE,"E20.left"),sQuery(id+"F0.wireOp",EDGE,"E20.right"),sQuery(id+"F0.wireOp",EDGE,"E33.bottom"),sQuery(id+"F0.wireOp",EDGE,"E33.top"),sQuery(id+"F0.wireOp",EDGE,"E34.left"),sQuery(id+"F0.wireOp",EDGE,"E34.right"),sQuery(id+"F0.wireOp",EDGE,"E35.left"),sQuery(id+"F0.wireOp",EDGE,"E35.right"),sQuery(id+"F0.wireOp",EDGE,"E36.trimOffspring"),sQuery(id+"F0.wireOp",EDGE,"E37.trimOffspring"),sQuery(id+"F0.wireOp",EDGE,"E38.trimOffspring"),sQuery(id+"F0.wireOp",EDGE,"E39.trimOffspring"),sQuery(id+"F0.wireOp",EDGE,"E40.trimOffspring"),sQuery(id+"F0.wireOp",EDGE,"E41.trimOffspring"),sQuery(id+"F0.wireOp",EDGE,"E42.trimOffspring"),sQuery(id+"F0.wireOp",EDGE,"E43.trimOffspring"),sQuery(id+"F0.wireOp",EDGE,"E44.bottom"),sQuery(id+"F0.wireOp",EDGE,"E44.top"),sQuery(id+"F0.wireOp",EDGE,"E44.left"),sQuery(id+"F0.wireOp",EDGE,"E44.right"),sQuery(id+"F0.wireOp",EDGE,"E45.bottom"),sQuery(id+"F0.wireOp",EDGE,"E45.top"),sQuery(id+"F0.wireOp",EDGE,"E45.left"),sQuery(id+"F0.wireOp",EDGE,"E45.right"),sQuery(id+"F0.wireOp",EDGE,"7093700b-8509-4908-bad7-ce82e1b1d340.1.0.0"),sQuery(id+"F0.wireOp",EDGE,"7093700b-8509-4908-bad7-ce82e1b1d340.1.0.2"),sQuery(id+"F0.wireOp",EDGE,"7093700b-8509-4908-bad7-ce82e1b1d340.1.0.3"),sQuery(id+"F0.wireOp",EDGE,"7093700b-8509-4908-bad7-ce82e1b1d340.1.0.5"),sQuery(id+"F0.wireOp",EDGE,"7093700b-8509-4908-bad7-ce82e1b1d340.1.0.6"),sQuery(id+"F0.wireOp",EDGE,"7093700b-8509-4908-bad7-ce82e1b1d340.1.0.7"),sQuery(id+"F0.wireOp",EDGE,"7093700b-8509-4908-bad7-ce82e1b1d340.1.0.8"),sQuery(id+"F0.wireOp",EDGE,"7093700b-8509-4908-bad7-ce82e1b1d340.1.0.9"),sQuery(id+"F0.wireOp",EDGE,"7093700b-8509-4908-bad7-ce82e1b1d340.1.0.12"),sQuery(id+"F0.wireOp",EDGE,"7093700b-8509-4908-bad7-ce82e1b1d340.1.0.13"),sQuery(id+"F0.wireOp",EDGE,"7093700b-8509-4908-bad7-ce82e1b1d340.1.0.14"),sQuery(id+"F0.wireOp",EDGE,"7093700b-8509-4908-bad7-ce82e1b1d340.1.0.15"),sQuery(id+"F0.wireOp",EDGE,"7093700b-8509-4908-bad7-ce82e1b1d340.1.0.16"),sQuery(id+"F0.wireOp",EDGE,"7093700b-8509-4908-bad7-ce82e1b1d340.1.0.17"),sQuery(id+"F0.wireOp",EDGE,"7093700b-8509-4908-bad7-ce82e1b1d340.1.0.18"),sQuery(id+"F0.wireOp",EDGE,"7093700b-8509-4908-bad7-ce82e1b1d340.1.0.19"),sQuery(id+"F0.wireOp",EDGE,"7093700b-8509-4908-bad7-ce82e1b1d340.1.0.20"),sQuery(id+"F0.wireOp",EDGE,"7093700b-8509-4908-bad7-ce82e1b1d340.1.0.21"),sQuery(id+"F0.wireOp",EDGE,"7093700b-8509-4908-bad7-ce82e1b1d340.2.0.0"),sQuery(id+"F0.wireOp",EDGE,"7093700b-8509-4908-bad7-ce82e1b1d340.2.0.2"),sQuery(id+"F0.wireOp",EDGE,"7093700b-8509-4908-bad7-ce82e1b1d340.2.0.3"),sQuery(id+"F0.wireOp",EDGE,"7093700b-8509-4908-bad7-ce82e1b1d340.2.0.5"),sQuery(id+"F0.wireOp",EDGE,"7093700b-8509-4908-bad7-ce82e1b1d340.2.0.6"),sQuery(id+"F0.wireOp",EDGE,"7093700b-8509-4908-bad7-ce82e1b1d340.2.0.7"),sQuery(id+"F0.wireOp",EDGE,"7093700b-8509-4908-bad7-ce82e1b1d340.2.0.8"),sQuery(id+"F0.wireOp",EDGE,"7093700b-8509-4908-bad7-ce82e1b1d340.2.0.9"),sQuery(id+"F0.wireOp",EDGE,"7093700b-8509-4908-bad7-ce82e1b1d340.2.0.12"),sQuery(id+"F0.wireOp",EDGE,"7093700b-8509-4908-bad7-ce82e1b1d340.2.0.13"),sQuery(id+"F0.wireOp",EDGE,"7093700b-8509-4908-bad7-ce82e1b1d340.2.0.14"),sQuery(id+"F0.wireOp",EDGE,"7093700b-8509-4908-bad7-ce82e1b1d340.2.0.15"),sQuery(id+"F0.wireOp",EDGE,"7093700b-8509-4908-bad7-ce82e1b1d340.2.0.16"),sQuery(id+"F0.wireOp",EDGE,"7093700b-8509-4908-bad7-ce82e1b1d340.2.0.17"),sQuery(id+"F0.wireOp",EDGE,"7093700b-8509-4908-bad7-ce82e1b1d340.2.0.18"),sQuery(id+"F0.wireOp",EDGE,"7093700b-8509-4908-bad7-ce82e1b1d340.2.0.19"),sQuery(id+"F0.wireOp",EDGE,"7093700b-8509-4908-bad7-ce82e1b1d340.2.0.20"),sQuery(id+"F0.wireOp",EDGE,"7093700b-8509-4908-bad7-ce82e1b1d340.2.0.21"),sQuery(id+"F0.wireOp",EDGE,"c973f7c2-3bf7-4545-afce-7af64f458de9.1.0.0"),sQuery(id+"F0.wireOp",EDGE,"c973f7c2-3bf7-4545-afce-7af64f458de9.1.0.1"),sQuery(id+"F0.wireOp",EDGE,"c973f7c2-3bf7-4545-afce-7af64f458de9.1.0.2"),sQuery(id+"F0.wireOp",EDGE,"c973f7c2-3bf7-4545-afce-7af64f458de9.1.0.4"),sQuery(id+"F0.wireOp",EDGE,"c973f7c2-3bf7-4545-afce-7af64f458de9.1.0.6"),sQuery(id+"F0.wireOp",EDGE,"c973f7c2-3bf7-4545-afce-7af64f458de9.1.0.7"),sQuery(id+"F0.wireOp",EDGE,"c973f7c2-3bf7-4545-afce-7af64f458de9.1.0.9"),sQuery(id+"F0.wireOp",EDGE,"c973f7c2-3bf7-4545-afce-7af64f458de9.1.0.10"),sQuery(id+"F0.wireOp",EDGE,"c973f7c2-3bf7-4545-afce-7af64f458de9.1.0.12"),sQuery(id+"F0.wireOp",EDGE,"c973f7c2-3bf7-4545-afce-7af64f458de9.1.0.14"),sQuery(id+"F0.wireOp",EDGE,"c973f7c2-3bf7-4545-afce-7af64f458de9.1.0.16"),sQuery(id+"F0.wireOp",EDGE,"c973f7c2-3bf7-4545-afce-7af64f458de9.1.0.18"),sQuery(id+"F0.wireOp",EDGE,"c973f7c2-3bf7-4545-afce-7af64f458de9.1.0.19"),sQuery(id+"F0.wireOp",EDGE,"c973f7c2-3bf7-4545-afce-7af64f458de9.1.0.20"),sQuery(id+"F0.wireOp",EDGE,"c973f7c2-3bf7-4545-afce-7af64f458de9.1.0.26"),sQuery(id+"F0.wireOp",EDGE,"c973f7c2-3bf7-4545-afce-7af64f458de9.1.0.28"),sQuery(id+"F0.wireOp",EDGE,"c973f7c2-3bf7-4545-afce-7af64f458de9.1.0.29"),sQuery(id+"F0.wireOp",EDGE,"c973f7c2-3bf7-4545-afce-7af64f458de9.1.0.30"),sQuery(id+"F0.wireOp",EDGE,"c973f7c2-3bf7-4545-afce-7af64f458de9.2.0.0"),sQuery(id+"F0.wireOp",EDGE,"c973f7c2-3bf7-4545-afce-7af64f458de9.2.0.1"),sQuery(id+"F0.wireOp",EDGE,"c973f7c2-3bf7-4545-afce-7af64f458de9.2.0.2"),sQuery(id+"F0.wireOp",EDGE,"c973f7c2-3bf7-4545-afce-7af64f458de9.2.0.4"),sQuery(id+"F0.wireOp",EDGE,"c973f7c2-3bf7-4545-afce-7af64f458de9.2.0.6"),sQuery(id+"F0.wireOp",EDGE,"c973f7c2-3bf7-4545-afce-7af64f458de9.2.0.7"),sQuery(id+"F0.wireOp",EDGE,"c973f7c2-3bf7-4545-afce-7af64f458de9.2.0.9"),sQuery(id+"F0.wireOp",EDGE,"c973f7c2-3bf7-4545-afce-7af64f458de9.2.0.10"),sQuery(id+"F0.wireOp",EDGE,"c973f7c2-3bf7-4545-afce-7af64f458de9.2.0.12"),sQuery(id+"F0.wireOp",EDGE,"c973f7c2-3bf7-4545-afce-7af64f458de9.2.0.14"),sQuery(id+"F0.wireOp",EDGE,"c973f7c2-3bf7-4545-afce-7af64f458de9.2.0.16"),sQuery(id+"F0.wireOp",EDGE,"c973f7c2-3bf7-4545-afce-7af64f458de9.2.0.18"),sQuery(id+"F0.wireOp",EDGE,"c973f7c2-3bf7-4545-afce-7af64f458de9.2.0.19"),sQuery(id+"F0.wireOp",EDGE,"c973f7c2-3bf7-4545-afce-7af64f458de9.2.0.20"),sQuery(id+"F0.wireOp",EDGE,"c973f7c2-3bf7-4545-afce-7af64f458de9.2.0.26"),sQuery(id+"F0.wireOp",EDGE,"c973f7c2-3bf7-4545-afce-7af64f458de9.2.0.28"),sQuery(id+"F0.wireOp",EDGE,"c973f7c2-3bf7-4545-afce-7af64f458de9.2.0.29"),sQuery(id+"F0.wireOp",EDGE,"c973f7c2-3bf7-4545-afce-7af64f458de9.2.0.30"),sQuery(id+"F0.wireOp",EDGE,"E46.left"),sQuery(id+"F0.wireOp",EDGE,"E46.right"),sQuery(id+"F0.wireOp",EDGE,"E47.left"),sQuery(id+"F0.wireOp",EDGE,"E47.right"),sQuery(id+"F0.wireOp",EDGE,"E48"),sQuery(id+"F0.wireOp",EDGE,"E49"),sQuery(id+"F0.wireOp",EDGE,"E50"),sQuery(id+"F0.wireOp",EDGE,"E51")])],"isStart":false});
            var sketch = newSketch(context, id + "F26", { "sketchPlane" : qUnion([Q0])});
            skLineSegment(sketch, "E147.bottom", {"start": v(-149.5, 17.96) * mm, "end": v(-139.5, 17.96) * mm});
            skLineSegment(sketch, "E147.top", {"start": v(-149.5, -57.04) * mm, "end": v(-139.5, -57.04) * mm});
            skLineSegment(sketch, "E147.left", {"start": v(-149.5, 17.96) * mm, "end": v(-149.5, -57.04) * mm});
            skLineSegment(sketch, "E147.right", {"start": v(-139.5, 17.96) * mm, "end": v(-139.5, -57.04) * mm});
            skLineSegment(sketch, "E148.bottom", {"start": v(0.5, -57.04) * mm, "end": v(-9.5, -57.04) * mm});
            skLineSegment(sketch, "E148.top", {"start": v(0.5, 17.96) * mm, "end": v(-9.5, 17.96) * mm});
            skLineSegment(sketch, "E148.left", {"start": v(0.5, -57.04) * mm, "end": v(0.5, 17.96) * mm});
            skLineSegment(sketch, "E148.right", {"start": v(-9.5, -57.04) * mm, "end": v(-9.5, 17.96) * mm});
            skSolve(sketch);
        }
        {
            var Q0;
            Q0=makeQuery(id+"F26.imprint","IMPRINT",FACE,{"disambiguationData":[TD([[makeQuery(id+"F26.imprint","IMPRINT",EDGE,{"derivedFrom":sQuery(id+"F26.wireOp",EDGE,"E148.bottom")}),-1.0]])]});
            var Q1;
            Q1=makeQuery(id+"F26.imprint","IMPRINT",FACE,{"disambiguationData":[TD([[makeQuery(id+"F26.imprint","IMPRINT",EDGE,{"derivedFrom":sQuery(id+"F26.wireOp",EDGE,"E147.bottom")}),1.0]])]});
            extrude(context, id + "F27", {"entities" : qUnion([Q0, Q1]), "operationType" : NewBodyOperationType.ADD, "depth" : 4 * mm});
        }
        {
            var Q0;
            {var subQ0=sQuery(id+"F0.wireOp",EDGE,"E0.bottom");Q0=makeQuery(id+"F27.boolean.opBoolean","MERGE",FACE,{"derivedFrom":[makeQuery(id+"FcxvOkpkAmDw7ie_3.boolean.opBoolean","MERGE",FACE,{"derivedFrom":[makeQuery(id+"F3.boolean.opBoolean","MERGE",FACE,{"derivedFrom":[makeQuery(id+"F2.opExtrude","SWEPT_FACE",FACE,{"disambiguationData":[OSD([subQ0])]}),makeQuery(id+"F3.opExtrude","SWEPT_FACE",FACE,{"disambiguationData":[OSD([subQ0])]})]}),makeQuery(id+"FcxvOkpkAmDw7ie_3.opExtrude","SWEPT_FACE",FACE,{"disambiguationData":[OSD([sQuery(id+"FNICA6uDXxchBR6_3.wireOp",EDGE,"OznuT0um-5Ypx-SHlm-bkf4-iYFOqL2Sfz4i.bottom")])]})]}),makeQuery(id+"F27.opExtrude","SWEPT_FACE",FACE,{"disambiguationData":[OSD([sQuery(id+"F26.wireOp",EDGE,"E147.top")])]}),makeQuery(id+"F27.opExtrude","SWEPT_FACE",FACE,{"disambiguationData":[OSD([sQuery(id+"F26.wireOp",EDGE,"E148.bottom")])]})]});}
            var sketch = newSketch(context, id + "F28", { "sketchPlane" : qUnion([Q0])});
            skLineSegment(sketch, "E149.bottom", {"start": v(-149.5, 0) * mm, "end": v(-141.5, 0) * mm});
            skLineSegment(sketch, "E149.top", {"start": v(-149.5, 7) * mm, "end": v(-141.5, 7) * mm});
            skLineSegment(sketch, "E149.left", {"start": v(-149.5, 0) * mm, "end": v(-149.5, 7) * mm});
            skLineSegment(sketch, "E149.right", {"start": v(-141.5, 0) * mm, "end": v(-141.5, 7) * mm});
            skLineSegment(sketch, "E150.bottom", {"start": v(0.5, 0) * mm, "end": v(-7.5, 0) * mm});
            skLineSegment(sketch, "E150.top", {"start": v(0.5, 7) * mm, "end": v(-7.5, 7) * mm});
            skLineSegment(sketch, "E150.left", {"start": v(0.5, 0) * mm, "end": v(0.5, 7) * mm});
            skLineSegment(sketch, "E150.right", {"start": v(-7.5, 0) * mm, "end": v(-7.5, 7) * mm});
            skSolve(sketch);
        }
        {
            var Q0;
            Q0=qSketchRegion(id+"F28",true);
            extrude(context, id + "F29", {"entities" : qUnion([Q0]), "operationType" : NewBodyOperationType.REMOVE, "oppositeDirection" : true, "depth" : 77.8 * mm});
        }
        {
            var Q0;
            {var subQ0=sQuery(id+"F0.wireOp",EDGE,"E0.right");var subQ1=sQuery(id+"F0.wireOp",EDGE,"E0.top");var subQ3=sQuery(id+"F0.wireOp",EDGE,"E0.bottom");var subQ5=sQuery(id+"F0.wireOp",EDGE,"E49");var subQ6=sQuery(id+"F0.wireOp",EDGE,"E48");var subQ7=sQuery(id+"F0.wireOp",EDGE,"E47.right");var subQ8=sQuery(id+"F0.wireOp",EDGE,"E47.left");var subQ9=sQuery(id+"F0.wireOp",EDGE,"E46.right");var subQ10=sQuery(id+"F0.wireOp",EDGE,"E46.left");var subQ11=sQuery(id+"F0.wireOp",EDGE,"c973f7c2-3bf7-4545-afce-7af64f458de9.2.0.30");var subQ12=sQuery(id+"F0.wireOp",EDGE,"c973f7c2-3bf7-4545-afce-7af64f458de9.2.0.0");var subQ13=sQuery(id+"F0.wireOp",EDGE,"c973f7c2-3bf7-4545-afce-7af64f458de9.2.0.29");var subQ16=sQuery(id+"F0.wireOp",EDGE,"c973f7c2-3bf7-4545-afce-7af64f458de9.2.0.10");var subQ17=sQuery(id+"F0.wireOp",EDGE,"c973f7c2-3bf7-4545-afce-7af64f458de9.2.0.28");var subQ20=sQuery(id+"F0.wireOp",EDGE,"c973f7c2-3bf7-4545-afce-7af64f458de9.2.0.18");var subQ21=sQuery(id+"F0.wireOp",EDGE,"c973f7c2-3bf7-4545-afce-7af64f458de9.2.0.26");var subQ24=sQuery(id+"F0.wireOp",EDGE,"c973f7c2-3bf7-4545-afce-7af64f458de9.2.0.1");var subQ25=sQuery(id+"F0.wireOp",EDGE,"c973f7c2-3bf7-4545-afce-7af64f458de9.2.0.19");var subQ27=sQuery(id+"F0.wireOp",EDGE,"c973f7c2-3bf7-4545-afce-7af64f458de9.2.0.9");var subQ30=sQuery(id+"F0.wireOp",EDGE,"c973f7c2-3bf7-4545-afce-7af64f458de9.2.0.4");var subQ34=sQuery(id+"F0.wireOp",EDGE,"c973f7c2-3bf7-4545-afce-7af64f458de9.2.0.2");var subQ35=sQuery(id+"F0.wireOp",EDGE,"c973f7c2-3bf7-4545-afce-7af64f458de9.2.0.7");var subQ37=sQuery(id+"F0.wireOp",EDGE,"c973f7c2-3bf7-4545-afce-7af64f458de9.2.0.16");var subQ39=sQuery(id+"F0.wireOp",EDGE,"c973f7c2-3bf7-4545-afce-7af64f458de9.2.0.20");var subQ41=sQuery(id+"F0.wireOp",EDGE,"c973f7c2-3bf7-4545-afce-7af64f458de9.2.0.12");var subQ43=sQuery(id+"F0.wireOp",EDGE,"c973f7c2-3bf7-4545-afce-7af64f458de9.2.0.14");var subQ44=sQuery(id+"F0.wireOp",EDGE,"c973f7c2-3bf7-4545-afce-7af64f458de9.2.0.6");var subQ45=sQuery(id+"F0.wireOp",EDGE,"c973f7c2-3bf7-4545-afce-7af64f458de9.1.0.30");var subQ46=sQuery(id+"F0.wireOp",EDGE,"c973f7c2-3bf7-4545-afce-7af64f458de9.1.0.0");var subQ47=sQuery(id+"F0.wireOp",EDGE,"c973f7c2-3bf7-4545-afce-7af64f458de9.1.0.29");var subQ50=sQuery(id+"F0.wireOp",EDGE,"c973f7c2-3bf7-4545-afce-7af64f458de9.1.0.10");var subQ51=sQuery(id+"F0.wireOp",EDGE,"c973f7c2-3bf7-4545-afce-7af64f458de9.1.0.28");var subQ54=sQuery(id+"F0.wireOp",EDGE,"c973f7c2-3bf7-4545-afce-7af64f458de9.1.0.18");var subQ55=sQuery(id+"F0.wireOp",EDGE,"c973f7c2-3bf7-4545-afce-7af64f458de9.1.0.26");var subQ58=sQuery(id+"F0.wireOp",EDGE,"c973f7c2-3bf7-4545-afce-7af64f458de9.1.0.1");var subQ59=sQuery(id+"F0.wireOp",EDGE,"c973f7c2-3bf7-4545-afce-7af64f458de9.1.0.19");var subQ61=sQuery(id+"F0.wireOp",EDGE,"c973f7c2-3bf7-4545-afce-7af64f458de9.1.0.9");var subQ64=sQuery(id+"F0.wireOp",EDGE,"c973f7c2-3bf7-4545-afce-7af64f458de9.1.0.4");var subQ68=sQuery(id+"F0.wireOp",EDGE,"c973f7c2-3bf7-4545-afce-7af64f458de9.1.0.2");var subQ69=sQuery(id+"F0.wireOp",EDGE,"c973f7c2-3bf7-4545-afce-7af64f458de9.1.0.7");var subQ71=sQuery(id+"F0.wireOp",EDGE,"c973f7c2-3bf7-4545-afce-7af64f458de9.1.0.16");var subQ73=sQuery(id+"F0.wireOp",EDGE,"c973f7c2-3bf7-4545-afce-7af64f458de9.1.0.20");var subQ75=sQuery(id+"F0.wireOp",EDGE,"c973f7c2-3bf7-4545-afce-7af64f458de9.1.0.12");var subQ77=sQuery(id+"F0.wireOp",EDGE,"c973f7c2-3bf7-4545-afce-7af64f458de9.1.0.14");var subQ78=sQuery(id+"F0.wireOp",EDGE,"c973f7c2-3bf7-4545-afce-7af64f458de9.1.0.6");var subQ79=sQuery(id+"F0.wireOp",EDGE,"7093700b-8509-4908-bad7-ce82e1b1d340.2.0.21");var subQ81=sQuery(id+"F0.wireOp",EDGE,"7093700b-8509-4908-bad7-ce82e1b1d340.2.0.20");var subQ82=sQuery(id+"F0.wireOp",EDGE,"7093700b-8509-4908-bad7-ce82e1b1d340.2.0.12");var subQ83=sQuery(id+"F0.wireOp",EDGE,"7093700b-8509-4908-bad7-ce82e1b1d340.2.0.15");var subQ86=sQuery(id+"F0.wireOp",EDGE,"7093700b-8509-4908-bad7-ce82e1b1d340.2.0.13");var subQ87=sQuery(id+"F0.wireOp",EDGE,"7093700b-8509-4908-bad7-ce82e1b1d340.2.0.17");var subQ90=sQuery(id+"F0.wireOp",EDGE,"7093700b-8509-4908-bad7-ce82e1b1d340.2.0.19");var subQ91=sQuery(id+"F0.wireOp",EDGE,"7093700b-8509-4908-bad7-ce82e1b1d340.2.0.18");var subQ93=sQuery(id+"F0.wireOp",EDGE,"7093700b-8509-4908-bad7-ce82e1b1d340.2.0.16");var subQ97=sQuery(id+"F0.wireOp",EDGE,"7093700b-8509-4908-bad7-ce82e1b1d340.2.0.2");var subQ99=sQuery(id+"F0.wireOp",EDGE,"7093700b-8509-4908-bad7-ce82e1b1d340.2.0.3");var subQ102=sQuery(id+"F0.wireOp",EDGE,"7093700b-8509-4908-bad7-ce82e1b1d340.2.0.0");var subQ104=sQuery(id+"F0.wireOp",EDGE,"7093700b-8509-4908-bad7-ce82e1b1d340.2.0.5");var subQ105=sQuery(id+"F0.wireOp",EDGE,"7093700b-8509-4908-bad7-ce82e1b1d340.2.0.14");var subQ108=sQuery(id+"F0.wireOp",EDGE,"7093700b-8509-4908-bad7-ce82e1b1d340.2.0.6");var subQ110=sQuery(id+"F0.wireOp",EDGE,"7093700b-8509-4908-bad7-ce82e1b1d340.2.0.9");var subQ111=sQuery(id+"F0.wireOp",EDGE,"7093700b-8509-4908-bad7-ce82e1b1d340.2.0.8");var subQ112=sQuery(id+"F0.wireOp",EDGE,"7093700b-8509-4908-bad7-ce82e1b1d340.2.0.7");var subQ113=sQuery(id+"F0.wireOp",EDGE,"E35.left");var subQ114=sQuery(id+"F0.wireOp",EDGE,"E34.right");var subQ115=sQuery(id+"F0.wireOp",EDGE,"E34.left");var subQ116=sQuery(id+"F0.wireOp",EDGE,"E33.top");var subQ117=sQuery(id+"F0.wireOp",EDGE,"E33.bottom");var subQ118=sQuery(id+"F0.wireOp",EDGE,"E20.right");var subQ119=sQuery(id+"F0.wireOp",EDGE,"E20.top");var subQ121=sQuery(id+"F0.wireOp",EDGE,"E37.trimOffspring");var subQ124=sQuery(id+"F0.wireOp",EDGE,"E20.bottom");var subQ126=sQuery(id+"F0.wireOp",EDGE,"E39.trimOffspring");var subQ128=sQuery(id+"F0.wireOp",EDGE,"E20.left");var subQ132=sQuery(id+"F0.wireOp",EDGE,"E36.trimOffspring");var subQ135=sQuery(id+"F0.wireOp",EDGE,"E28.trimOffspring");var subQ136=sQuery(id+"F0.wireOp",EDGE,"E42.trimOffspring");var subQ139=sQuery(id+"F0.wireOp",EDGE,"E27.trimOffspring");var subQ142=sQuery(id+"F0.wireOp",EDGE,"E25.trimOffspring");var subQ146=sQuery(id+"F0.wireOp",EDGE,"E24.trimOffspring");var subQ147=sQuery(id+"F0.wireOp",EDGE,"E31.trimOffspring");var subQ148=sQuery(id+"F0.wireOp",EDGE,"E23.right");var subQ149=sQuery(id+"F0.wireOp",EDGE,"E30.trimOffspring");var subQ150=sQuery(id+"F0.wireOp",EDGE,"E23.left");var subQ151=sQuery(id+"F0.wireOp",EDGE,"E29.trimOffspring");var subQ152=sQuery(id+"F0.wireOp",EDGE,"E22.right");var subQ153=sQuery(id+"F0.wireOp",EDGE,"E22.left");var subQ154=sQuery(id+"F0.wireOp",EDGE,"E21.top");var subQ155=sQuery(id+"F0.wireOp",EDGE,"E26.trimOffspring");var subQ156=sQuery(id+"F0.wireOp",EDGE,"E21.bottom");var subQ157=sQuery(id+"F0.wireOp",EDGE,"E19.right");var subQ158=sQuery(id+"F0.wireOp",EDGE,"E19.top");var subQ162=sQuery(id+"F0.wireOp",EDGE,"E19.bottom");var subQ165=sQuery(id+"F0.wireOp",EDGE,"E15.top");var subQ168=sQuery(id+"F0.wireOp",EDGE,"E15.bottom");var subQ171=sQuery(id+"F0.wireOp",EDGE,"E35.right");var subQ174=sQuery(id+"F0.wireOp",EDGE,"7093700b-8509-4908-bad7-ce82e1b1d340.1.0.16");var subQ175=sQuery(id+"F0.wireOp",EDGE,"E15.right");var subQ176=sQuery(id+"F0.wireOp",EDGE,"E15.left");var subQ177=sQuery(id+"F0.wireOp",EDGE,"E19.left");var subQ180=sQuery(id+"F0.wireOp",EDGE,"E38.trimOffspring");var subQ181=sQuery(id+"F0.wireOp",EDGE,"E40.trimOffspring");var subQ185=sQuery(id+"F0.wireOp",EDGE,"7093700b-8509-4908-bad7-ce82e1b1d340.1.0.17");var subQ186=sQuery(id+"F0.wireOp",EDGE,"7093700b-8509-4908-bad7-ce82e1b1d340.1.0.20");var subQ193=sQuery(id+"F0.wireOp",EDGE,"7093700b-8509-4908-bad7-ce82e1b1d340.1.0.19");var subQ200=sQuery(id+"F0.wireOp",EDGE,"E41.trimOffspring");var subQ201=sQuery(id+"F0.wireOp",EDGE,"E43.trimOffspring");var subQ202=sQuery(id+"F0.wireOp",EDGE,"E44.left");var subQ203=sQuery(id+"F0.wireOp",EDGE,"E44.bottom");var subQ206=sQuery(id+"F0.wireOp",EDGE,"E44.right");var subQ208=sQuery(id+"F0.wireOp",EDGE,"E44.top");var subQ212=sQuery(id+"F0.wireOp",EDGE,"E45.left");var subQ213=sQuery(id+"F0.wireOp",EDGE,"E45.bottom");var subQ216=sQuery(id+"F0.wireOp",EDGE,"E45.right");var subQ218=sQuery(id+"F0.wireOp",EDGE,"E45.top");var subQ222=sQuery(id+"F0.wireOp",EDGE,"7093700b-8509-4908-bad7-ce82e1b1d340.1.0.0");var subQ223=sQuery(id+"F0.wireOp",EDGE,"7093700b-8509-4908-bad7-ce82e1b1d340.1.0.2");var subQ226=sQuery(id+"F0.wireOp",EDGE,"7093700b-8509-4908-bad7-ce82e1b1d340.1.0.9");var subQ228=sQuery(id+"F0.wireOp",EDGE,"7093700b-8509-4908-bad7-ce82e1b1d340.1.0.15");var subQ230=sQuery(id+"F0.wireOp",EDGE,"7093700b-8509-4908-bad7-ce82e1b1d340.1.0.8");var subQ232=sQuery(id+"F0.wireOp",EDGE,"7093700b-8509-4908-bad7-ce82e1b1d340.1.0.3");var subQ233=sQuery(id+"F0.wireOp",EDGE,"7093700b-8509-4908-bad7-ce82e1b1d340.1.0.5");var subQ234=sQuery(id+"F0.wireOp",EDGE,"7093700b-8509-4908-bad7-ce82e1b1d340.1.0.6");var subQ235=sQuery(id+"F0.wireOp",EDGE,"7093700b-8509-4908-bad7-ce82e1b1d340.1.0.7");var subQ236=sQuery(id+"F0.wireOp",EDGE,"7093700b-8509-4908-bad7-ce82e1b1d340.1.0.12");var subQ237=sQuery(id+"F0.wireOp",EDGE,"7093700b-8509-4908-bad7-ce82e1b1d340.1.0.13");var subQ238=sQuery(id+"F0.wireOp",EDGE,"7093700b-8509-4908-bad7-ce82e1b1d340.1.0.14");var subQ246=sQuery(id+"F0.wireOp",EDGE,"7093700b-8509-4908-bad7-ce82e1b1d340.1.0.18");var subQ251=sQuery(id+"F0.wireOp",EDGE,"7093700b-8509-4908-bad7-ce82e1b1d340.1.0.21");var subQ255=sQuery(id+"F0.wireOp",EDGE,"E51");var subQ256=sQuery(id+"F0.wireOp",EDGE,"E50");var subQ257=sQuery(id+"F0.wireOp",EDGE,"E0.left");var subQ258=makeQuery(id+"F2.opExtrude","CAP_FACE",FACE,{"disambiguationData":[OSD([subQ3,subQ1,subQ257,subQ0,sQuery(id+"F0.wireOp",EDGE,"E3"),sQuery(id+"F0.wireOp",EDGE,"E4"),sQuery(id+"F0.wireOp",EDGE,"E5"),sQuery(id+"F0.wireOp",EDGE,"E8"),sQuery(id+"F0.wireOp",EDGE,"E9"),sQuery(id+"F0.wireOp",EDGE,"E10"),sQuery(id+"F0.wireOp",EDGE,"E11"),sQuery(id+"F0.wireOp",EDGE,"E12"),sQuery(id+"F0.wireOp",EDGE,"E13"),sQuery(id+"F0.wireOp",EDGE,"E14"),subQ168,subQ165,subQ176,subQ175,sQuery(id+"F0.wireOp",EDGE,"E16"),sQuery(id+"F0.wireOp",EDGE,"E17"),subQ162,subQ158,subQ177,subQ157,subQ156,subQ154,subQ153,subQ152,subQ150,subQ148,subQ146,subQ142,subQ155,subQ139,subQ135,subQ151,subQ149,subQ147,subQ124,subQ119,subQ128,subQ118,subQ117,subQ116,subQ115,subQ114,subQ113,subQ171,subQ132,subQ121,subQ180,subQ126,subQ181,subQ200,subQ136,subQ201,subQ203,subQ208,subQ202,subQ206,subQ213,subQ218,subQ212,subQ216,subQ222,subQ223,subQ232,subQ233,subQ234,subQ235,subQ230,subQ226,subQ236,subQ237,subQ238,subQ228,subQ174,subQ185,subQ246,subQ193,subQ186,subQ251,subQ102,subQ97,subQ99,subQ104,subQ108,subQ112,subQ111,subQ110,subQ82,subQ86,subQ105,subQ83,subQ93,subQ87,subQ91,subQ90,subQ81,subQ79,subQ46,subQ58,subQ68,subQ64,subQ78,subQ69,subQ61,subQ50,subQ75,subQ77,subQ71,subQ54,subQ59,subQ73,subQ55,subQ51,subQ47,subQ45,subQ12,subQ24,subQ34,subQ30,subQ44,subQ35,subQ27,subQ16,subQ41,subQ43,subQ37,subQ20,subQ25,subQ39,subQ21,subQ17,subQ13,subQ11,subQ10,subQ9,subQ8,subQ7,subQ6,subQ5,subQ256,subQ255])],"isStart":true});Q0=makeQuery(id+"FcxvOkpkAmDw7ie_3.boolean.opBoolean","MERGE",FACE,{"derivedFrom":[makeQuery(id+"F24.boolean.opBoolean","SPLIT",FACE,{"disambiguationData":[TD([makeQuery(id+"F2.opExtrude","SWEPT_FACE",FACE,{"disambiguationData":[OSD([subQ257])]})])],"derivedFrom":subQ258}),makeQuery(id+"F24.boolean.opBoolean","SPLIT",FACE,{"disambiguationData":[TD([makeQuery(id+"F2.opExtrude","SWEPT_FACE",FACE,{"disambiguationData":[OSD([subQ0])]})])],"derivedFrom":subQ258}),makeQuery(id+"FcxvOkpkAmDw7ie_3.opExtrude","CAP_FACE",FACE,{"disambiguationData":[OSD([sQuery(id+"FNICA6uDXxchBR6_3.wireOp",EDGE,"OznuT0um-5Ypx-SHlm-bkf4-iYFOqL2Sfz4i.bottom"),sQuery(id+"FNICA6uDXxchBR6_3.wireOp",EDGE,"OznuT0um-5Ypx-SHlm-bkf4-iYFOqL2Sfz4i.top"),sQuery(id+"FNICA6uDXxchBR6_3.wireOp",EDGE,"OznuT0um-5Ypx-SHlm-bkf4-iYFOqL2Sfz4i.left"),sQuery(id+"FNICA6uDXxchBR6_3.wireOp",EDGE,"OznuT0um-5Ypx-SHlm-bkf4-iYFOqL2Sfz4i.right")])],"isStart":false}),makeQuery(id+"FcxvOkpkAmDw7ie_3.opExtrude","CAP_FACE",FACE,{"disambiguationData":[OSD([sQuery(id+"FNICA6uDXxchBR6_3.wireOp",EDGE,"YSd4T3NJ-1L5Y-MwVD-52kg-DvB7oUMf2wlW.bottom"),sQuery(id+"FNICA6uDXxchBR6_3.wireOp",EDGE,"YSd4T3NJ-1L5Y-MwVD-52kg-DvB7oUMf2wlW.top"),sQuery(id+"FNICA6uDXxchBR6_3.wireOp",EDGE,"YSd4T3NJ-1L5Y-MwVD-52kg-DvB7oUMf2wlW.left"),sQuery(id+"FNICA6uDXxchBR6_3.wireOp",EDGE,"YSd4T3NJ-1L5Y-MwVD-52kg-DvB7oUMf2wlW.right")])],"isStart":false}),makeQuery(id+"FcxvOkpkAmDw7ie_3.opExtrude","CAP_FACE",FACE,{"disambiguationData":[OSD([sQuery(id+"FNICA6uDXxchBR6_3.wireOp",EDGE,"awoJ12up-LfxG-riiH-PCTd-TFvWrLSTyvKZ.bottom"),sQuery(id+"FNICA6uDXxchBR6_3.wireOp",EDGE,"awoJ12up-LfxG-riiH-PCTd-TFvWrLSTyvKZ.top"),sQuery(id+"FNICA6uDXxchBR6_3.wireOp",EDGE,"awoJ12up-LfxG-riiH-PCTd-TFvWrLSTyvKZ.left"),sQuery(id+"FNICA6uDXxchBR6_3.wireOp",EDGE,"awoJ12up-LfxG-riiH-PCTd-TFvWrLSTyvKZ.right")])],"isStart":false}),makeQuery(id+"FcxvOkpkAmDw7ie_3.opExtrude","CAP_FACE",FACE,{"disambiguationData":[OSD([sQuery(id+"FNICA6uDXxchBR6_3.wireOp",EDGE,"WfW6qyGR-5Y5B-en90-Dwp4-fLCMDk8WttTC.bottom"),sQuery(id+"FNICA6uDXxchBR6_3.wireOp",EDGE,"WfW6qyGR-5Y5B-en90-Dwp4-fLCMDk8WttTC.top"),sQuery(id+"FNICA6uDXxchBR6_3.wireOp",EDGE,"WfW6qyGR-5Y5B-en90-Dwp4-fLCMDk8WttTC.left"),sQuery(id+"FNICA6uDXxchBR6_3.wireOp",EDGE,"WfW6qyGR-5Y5B-en90-Dwp4-fLCMDk8WttTC.right")])],"isStart":false})]});}
            var sketch = newSketch(context, id + "F30", { "sketchPlane" : qUnion([Q0])});
            skLineSegment(sketch, "E151.bottom", {"start": v(-141.5, -17.96) * mm, "end": v(-7.5, -17.96) * mm});
            skLineSegment(sketch, "E151.top", {"start": v(-141.5, -15.46) * mm, "end": v(-7.5, -15.46) * mm});
            skLineSegment(sketch, "E151.left", {"start": v(-141.5, -17.96) * mm, "end": v(-141.5, -15.46) * mm});
            skLineSegment(sketch, "E151.right", {"start": v(-7.5, -17.96) * mm, "end": v(-7.5, -15.46) * mm});
            skSolve(sketch);
        }
        {
            var Q0;
            Q0=qSketchRegion(id+"F30",true);
            extrude(context, id + "F31", {"entities" : qUnion([Q0]), "operationType" : NewBodyOperationType.REMOVE, "oppositeDirection" : true, "depth" : 3 * mm});
        }
    });
